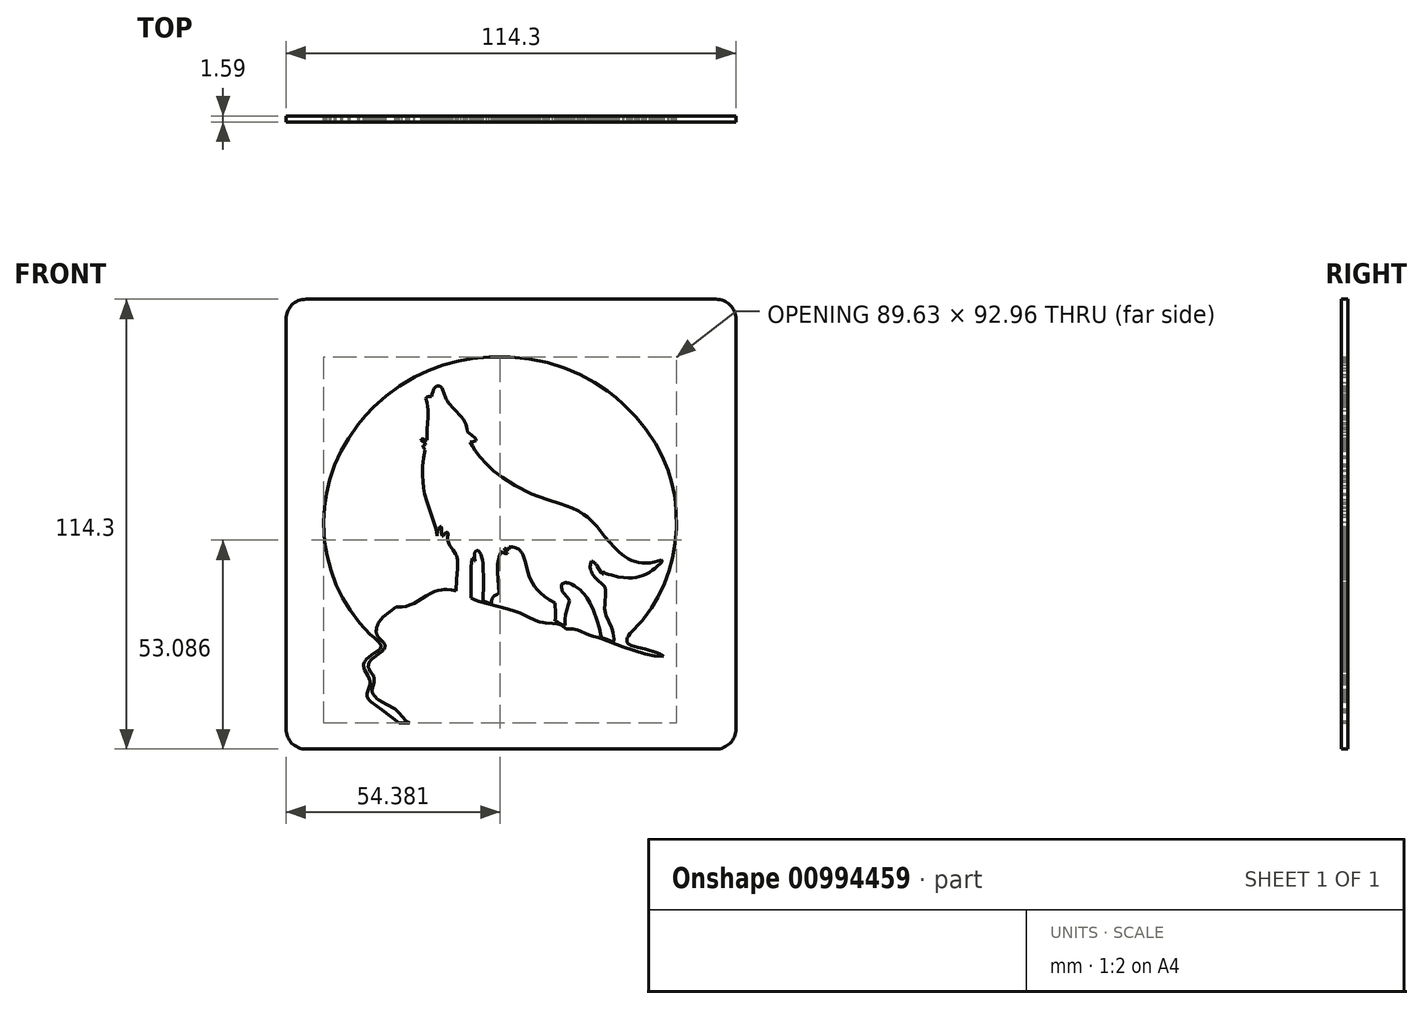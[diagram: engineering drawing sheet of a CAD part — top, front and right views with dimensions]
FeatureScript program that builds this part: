
annotation { "Feature Type Name" : "Feature", "Feature Type Description" : "" }
export const myFeature = defineFeature(function(context is Context, id is Id, definition is map)
    precondition{}
    {
        {
            var Q0;
            Q0=qCreatedBy(makeId("Front.planeOp"),FACE);
            var sketch = newSketch(context, id + "F0", { "sketchPlane" : qUnion([Q0])});
            skLineSegment(sketch, "E0", {"start": v(-50.8, -48.51) * mm, "end": v(-50.61, -48.95) * mm});
            skLineSegment(sketch, "E1", {"start": v(-50.61, -48.95) * mm, "end": v(-50.42, -49.3) * mm});
            skLineSegment(sketch, "E2", {"start": v(-50.42, -49.3) * mm, "end": v(-50.23, -49.58) * mm});
            skLineSegment(sketch, "E3", {"start": v(-50.23, -49.58) * mm, "end": v(-50.05, -49.8) * mm});
            skLineSegment(sketch, "E4", {"start": v(-50.05, -49.8) * mm, "end": v(-49.86, -49.99) * mm});
            skLineSegment(sketch, "E5", {"start": v(-49.86, -49.99) * mm, "end": v(-49.64, -50.16) * mm});
            skLineSegment(sketch, "E6", {"start": v(-49.64, -50.16) * mm, "end": v(-49.41, -50.32) * mm});
            skLineSegment(sketch, "E7", {"start": v(-49.41, -50.32) * mm, "end": v(-49.2, -50.43) * mm});
            skLineSegment(sketch, "E8", {"start": v(-49.2, -50.43) * mm, "end": v(-48.94, -50.55) * mm});
            skLineSegment(sketch, "E9", {"start": v(-48.94, -50.55) * mm, "end": v(-28.45, -50.55) * mm});
            skLineSegment(sketch, "E10", {"start": v(-28.45, -50.55) * mm, "end": v(-32.68, -47.16) * mm});
            skLineSegment(sketch, "E11", {"start": v(-32.68, -47.16) * mm, "end": v(-35.5, -45.2) * mm});
            skLineSegment(sketch, "E12", {"start": v(-35.5, -45.2) * mm, "end": v(-35.9, -44.8) * mm});
            skLineSegment(sketch, "E13", {"start": v(-35.9, -44.8) * mm, "end": v(-36.11, -44.55) * mm});
            skLineSegment(sketch, "E14", {"start": v(-36.11, -44.55) * mm, "end": v(-36.29, -44.28) * mm});
            skLineSegment(sketch, "E15", {"start": v(-36.29, -44.28) * mm, "end": v(-36.43, -44.01) * mm});
            skLineSegment(sketch, "E16", {"start": v(-36.43, -44.01) * mm, "end": v(-36.5, -43.82) * mm});
            skLineSegment(sketch, "E17", {"start": v(-36.5, -43.82) * mm, "end": v(-36.55, -43.63) * mm});
            skLineSegment(sketch, "E18", {"start": v(-36.55, -43.63) * mm, "end": v(-36.58, -43.43) * mm});
            skLineSegment(sketch, "E19", {"start": v(-36.58, -43.43) * mm, "end": v(-36.58, -43.32) * mm});
            skLineSegment(sketch, "E20", {"start": v(-36.58, -43.32) * mm, "end": v(-36.57, -43.15) * mm});
            skLineSegment(sketch, "E21", {"start": v(-36.57, -43.15) * mm, "end": v(-36.54, -42.98) * mm});
            skLineSegment(sketch, "E22", {"start": v(-36.54, -42.98) * mm, "end": v(-36.47, -42.67) * mm});
            skLineSegment(sketch, "E23", {"start": v(-36.47, -42.67) * mm, "end": v(-35.78, -40.74) * mm});
            skLineSegment(sketch, "E24", {"start": v(-35.78, -40.74) * mm, "end": v(-35.74, -40.48) * mm});
            skLineSegment(sketch, "E25", {"start": v(-35.74, -40.48) * mm, "end": v(-35.73, -40.35) * mm});
            skLineSegment(sketch, "E26", {"start": v(-35.73, -40.35) * mm, "end": v(-35.73, -40.22) * mm});
            skLineSegment(sketch, "E27", {"start": v(-35.73, -40.22) * mm, "end": v(-35.74, -40.05) * mm});
            skLineSegment(sketch, "E28", {"start": v(-35.74, -40.05) * mm, "end": v(-35.79, -39.8) * mm});
            skLineSegment(sketch, "E29", {"start": v(-35.79, -39.8) * mm, "end": v(-35.86, -39.53) * mm});
            skLineSegment(sketch, "E30", {"start": v(-35.86, -39.53) * mm, "end": v(-36, -39.18) * mm});
            skLineSegment(sketch, "E31", {"start": v(-36, -39.18) * mm, "end": v(-36.32, -38.57) * mm});
            skLineSegment(sketch, "E32", {"start": v(-36.32, -38.57) * mm, "end": v(-37.15, -37.06) * mm});
            skLineSegment(sketch, "E33", {"start": v(-37.15, -37.06) * mm, "end": v(-37.29, -36.7) * mm});
            skLineSegment(sketch, "E34", {"start": v(-37.29, -36.7) * mm, "end": v(-37.36, -36.44) * mm});
            skLineSegment(sketch, "E35", {"start": v(-37.36, -36.44) * mm, "end": v(-37.41, -36.17) * mm});
            skLineSegment(sketch, "E36", {"start": v(-37.41, -36.17) * mm, "end": v(-37.43, -36) * mm});
            skLineSegment(sketch, "E37", {"start": v(-37.43, -36) * mm, "end": v(-37.42, -35.82) * mm});
            skLineSegment(sketch, "E38", {"start": v(-37.42, -35.82) * mm, "end": v(-37.39, -35.56) * mm});
            skLineSegment(sketch, "E39", {"start": v(-37.39, -35.56) * mm, "end": v(-37.32, -35.3) * mm});
            skLineSegment(sketch, "E40", {"start": v(-37.32, -35.3) * mm, "end": v(-37.21, -35.07) * mm});
            skLineSegment(sketch, "E41", {"start": v(-37.21, -35.07) * mm, "end": v(-37.08, -34.84) * mm});
            skLineSegment(sketch, "E42", {"start": v(-37.08, -34.84) * mm, "end": v(-36.92, -34.62) * mm});
            skLineSegment(sketch, "E43", {"start": v(-36.92, -34.62) * mm, "end": v(-36.65, -34.3) * mm});
            skLineSegment(sketch, "E44", {"start": v(-36.65, -34.3) * mm, "end": v(-36.21, -33.9) * mm});
            skLineSegment(sketch, "E45", {"start": v(-36.21, -33.9) * mm, "end": v(-35.35, -33.26) * mm});
            skLineSegment(sketch, "E46", {"start": v(-35.35, -33.26) * mm, "end": v(-33.7, -32.09) * mm});
            skLineSegment(sketch, "E47", {"start": v(-33.7, -32.09) * mm, "end": v(-33.43, -31.84) * mm});
            skLineSegment(sketch, "E48", {"start": v(-33.43, -31.84) * mm, "end": v(-33.29, -31.68) * mm});
            skLineSegment(sketch, "E49", {"start": v(-33.29, -31.68) * mm, "end": v(-33.17, -31.5) * mm});
            skLineSegment(sketch, "E50", {"start": v(-33.17, -31.5) * mm, "end": v(-33.09, -31.34) * mm});
            skLineSegment(sketch, "E51", {"start": v(-33.09, -31.34) * mm, "end": v(-33.06, -31.25) * mm});
            skLineSegment(sketch, "E52", {"start": v(-33.06, -31.25) * mm, "end": v(-33.03, -31.16) * mm});
            skLineSegment(sketch, "E53", {"start": v(-33.03, -31.16) * mm, "end": v(-33.02, -31.07) * mm});
            skLineSegment(sketch, "E54", {"start": v(-33.02, -31.07) * mm, "end": v(-33.02, -31.02) * mm});
            skLineSegment(sketch, "E55", {"start": v(-33.02, -31.02) * mm, "end": v(-33.02, -30.96) * mm});
            skLineSegment(sketch, "E56", {"start": v(-33.02, -30.96) * mm, "end": v(-33.04, -30.85) * mm});
            skLineSegment(sketch, "E57", {"start": v(-33.04, -30.85) * mm, "end": v(-33.08, -30.73) * mm});
            skLineSegment(sketch, "E58", {"start": v(-33.08, -30.73) * mm, "end": v(-33.13, -30.6) * mm});
            skLineSegment(sketch, "E59", {"start": v(-33.13, -30.6) * mm, "end": v(-33.24, -30.42) * mm});
            skLineSegment(sketch, "E60", {"start": v(-33.24, -30.42) * mm, "end": v(-33.43, -30.16) * mm});
            skLineSegment(sketch, "E61", {"start": v(-33.43, -30.16) * mm, "end": v(-33.8, -29.75) * mm});
            skLineSegment(sketch, "E62", {"start": v(-33.8, -29.75) * mm, "end": v(-34.81, -28.83) * mm});
            skLineSegment(sketch, "E63", {"start": v(-34.81, -28.83) * mm, "end": v(-35.73, -28.03) * mm});
            skLineSegment(sketch, "E64", {"start": v(-35.73, -28.03) * mm, "end": v(-38.4, -25.1) * mm});
            skLineSegment(sketch, "E65", {"start": v(-38.4, -25.1) * mm, "end": v(-40.85, -21.83) * mm});
            skLineSegment(sketch, "E66", {"start": v(-40.85, -21.83) * mm, "end": v(-42.74, -18.74) * mm});
            skLineSegment(sketch, "E67", {"start": v(-42.74, -18.74) * mm, "end": v(-44.38, -15.4) * mm});
            skLineSegment(sketch, "E68", {"start": v(-44.38, -15.4) * mm, "end": v(-45.73, -11.78) * mm});
            skLineSegment(sketch, "E69", {"start": v(-45.73, -11.78) * mm, "end": v(-46.75, -7.92) * mm});
            skLineSegment(sketch, "E70", {"start": v(-46.75, -7.92) * mm, "end": v(-47.3, -4.5) * mm});
            skLineSegment(sketch, "E71", {"start": v(-47.3, -4.5) * mm, "end": v(-47.5, -2.36) * mm});
            skLineSegment(sketch, "E72", {"start": v(-47.5, -2.36) * mm, "end": v(-47.58, 0.6) * mm});
            skLineSegment(sketch, "E73", {"start": v(-47.58, 0.6) * mm, "end": v(-47.4, 4.31) * mm});
            skLineSegment(sketch, "E74", {"start": v(-47.4, 4.31) * mm, "end": v(-46.89, 7.85) * mm});
            skLineSegment(sketch, "E75", {"start": v(-46.89, 7.85) * mm, "end": v(-46.09, 11.2) * mm});
            skLineSegment(sketch, "E76", {"start": v(-46.09, 11.2) * mm, "end": v(-44.8, 15) * mm});
            skLineSegment(sketch, "E77", {"start": v(-44.8, 15) * mm, "end": v(-43.17, 18.54) * mm});
            skLineSegment(sketch, "E78", {"start": v(-43.17, 18.54) * mm, "end": v(-41.28, 21.81) * mm});
            skLineSegment(sketch, "E79", {"start": v(-41.28, 21.81) * mm, "end": v(-38.8, 25.31) * mm});
            skLineSegment(sketch, "E80", {"start": v(-38.8, 25.31) * mm, "end": v(-36.88, 27.6) * mm});
            skLineSegment(sketch, "E81", {"start": v(-36.88, 27.6) * mm, "end": v(-34.88, 29.72) * mm});
            skLineSegment(sketch, "E82", {"start": v(-34.88, 29.72) * mm, "end": v(-31.75, 32.55) * mm});
            skLineSegment(sketch, "E83", {"start": v(-31.75, 32.55) * mm, "end": v(-28.26, 35.12) * mm});
            skLineSegment(sketch, "E84", {"start": v(-28.26, 35.12) * mm, "end": v(-24.44, 37.37) * mm});
            skLineSegment(sketch, "E85", {"start": v(-24.44, 37.37) * mm, "end": v(-20.93, 39.02) * mm});
            skLineSegment(sketch, "E86", {"start": v(-20.93, 39.02) * mm, "end": v(-17.2, 40.39) * mm});
            skLineSegment(sketch, "E87", {"start": v(-17.2, 40.39) * mm, "end": v(-13.27, 41.43) * mm});
            skLineSegment(sketch, "E88", {"start": v(-13.27, 41.43) * mm, "end": v(-9.85, 42.03) * mm});
            skLineSegment(sketch, "E89", {"start": v(-9.85, 42.03) * mm, "end": v(-5.59, 42.42) * mm});
            skLineSegment(sketch, "E90", {"start": v(-5.59, 42.42) * mm, "end": v(-0.25, 42.41) * mm});
            skLineSegment(sketch, "E91", {"start": v(-0.25, 42.41) * mm, "end": v(4.72, 41.93) * mm});
            skLineSegment(sketch, "E92", {"start": v(4.72, 41.93) * mm, "end": v(9.34, 41.01) * mm});
            skLineSegment(sketch, "E93", {"start": v(9.34, 41.01) * mm, "end": v(13.62, 39.7) * mm});
            skLineSegment(sketch, "E94", {"start": v(13.62, 39.7) * mm, "end": v(17.58, 38.03) * mm});
            skLineSegment(sketch, "E95", {"start": v(17.58, 38.03) * mm, "end": v(21.23, 36.04) * mm});
            skLineSegment(sketch, "E96", {"start": v(21.23, 36.04) * mm, "end": v(24.58, 33.78) * mm});
            skLineSegment(sketch, "E97", {"start": v(24.58, 33.78) * mm, "end": v(26.66, 32.13) * mm});
            skLineSegment(sketch, "E98", {"start": v(26.66, 32.13) * mm, "end": v(28.62, 30.4) * mm});
            skLineSegment(sketch, "E99", {"start": v(28.62, 30.4) * mm, "end": v(31.78, 27.16) * mm});
            skLineSegment(sketch, "E100", {"start": v(31.78, 27.16) * mm, "end": v(34.36, 24) * mm});
            skLineSegment(sketch, "E101", {"start": v(34.36, 24) * mm, "end": v(36.69, 20.52) * mm});
            skLineSegment(sketch, "E102", {"start": v(36.69, 20.52) * mm, "end": v(38.43, 17.28) * mm});
            skLineSegment(sketch, "E103", {"start": v(38.43, 17.28) * mm, "end": v(39.88, 13.8) * mm});
            skLineSegment(sketch, "E104", {"start": v(39.88, 13.8) * mm, "end": v(40.84, 10.72) * mm});
            skLineSegment(sketch, "E105", {"start": v(40.84, 10.72) * mm, "end": v(41.54, 7.45) * mm});
            skLineSegment(sketch, "E106", {"start": v(41.54, 7.45) * mm, "end": v(41.82, 5.4) * mm});
            skLineSegment(sketch, "E107", {"start": v(41.82, 5.4) * mm, "end": v(42, 3.3) * mm});
            skLineSegment(sketch, "E108", {"start": v(42, 3.3) * mm, "end": v(42.05, -0.92) * mm});
            skLineSegment(sketch, "E109", {"start": v(42.05, -0.92) * mm, "end": v(41.73, -4.87) * mm});
            skLineSegment(sketch, "E110", {"start": v(41.73, -4.87) * mm, "end": v(41.1, -8.54) * mm});
            skLineSegment(sketch, "E111", {"start": v(41.1, -8.54) * mm, "end": v(40.17, -11.96) * mm});
            skLineSegment(sketch, "E112", {"start": v(40.17, -11.96) * mm, "end": v(39, -15.13) * mm});
            skLineSegment(sketch, "E113", {"start": v(39, -15.13) * mm, "end": v(37.35, -18.55) * mm});
            skLineSegment(sketch, "E114", {"start": v(37.35, -18.55) * mm, "end": v(35.75, -21.24) * mm});
            skLineSegment(sketch, "E115", {"start": v(35.75, -21.24) * mm, "end": v(33.7, -24.13) * mm});
            skLineSegment(sketch, "E116", {"start": v(33.7, -24.13) * mm, "end": v(33.34, -24.55) * mm});
            skLineSegment(sketch, "E117", {"start": v(33.34, -24.55) * mm, "end": v(30.29, -27.79) * mm});
            skLineSegment(sketch, "E118", {"start": v(30.29, -27.79) * mm, "end": v(29.84, -28.43) * mm});
            skLineSegment(sketch, "E119", {"start": v(29.84, -28.43) * mm, "end": v(29.64, -28.8) * mm});
            skLineSegment(sketch, "E120", {"start": v(29.64, -28.8) * mm, "end": v(29.54, -29.03) * mm});
            skLineSegment(sketch, "E121", {"start": v(29.54, -29.03) * mm, "end": v(29.47, -29.26) * mm});
            skLineSegment(sketch, "E122", {"start": v(29.47, -29.26) * mm, "end": v(29.44, -29.48) * mm});
            skLineSegment(sketch, "E123", {"start": v(29.44, -29.48) * mm, "end": v(29.43, -29.7) * mm});
            skLineSegment(sketch, "E124", {"start": v(29.43, -29.7) * mm, "end": v(29.44, -29.8) * mm});
            skLineSegment(sketch, "E125", {"start": v(29.44, -29.8) * mm, "end": v(29.46, -29.89) * mm});
            skLineSegment(sketch, "E126", {"start": v(29.46, -29.89) * mm, "end": v(29.49, -29.95) * mm});
            skLineSegment(sketch, "E127", {"start": v(29.49, -29.95) * mm, "end": v(29.51, -30.01) * mm});
            skLineSegment(sketch, "E128", {"start": v(29.51, -30.01) * mm, "end": v(29.58, -30.13) * mm});
            skLineSegment(sketch, "E129", {"start": v(29.58, -30.13) * mm, "end": v(29.68, -30.24) * mm});
            skLineSegment(sketch, "E130", {"start": v(29.68, -30.24) * mm, "end": v(29.8, -30.35) * mm});
            skLineSegment(sketch, "E131", {"start": v(29.8, -30.35) * mm, "end": v(29.93, -30.45) * mm});
            skLineSegment(sketch, "E132", {"start": v(29.93, -30.45) * mm, "end": v(30.17, -30.6) * mm});
            skLineSegment(sketch, "E133", {"start": v(30.17, -30.6) * mm, "end": v(30.53, -30.77) * mm});
            skLineSegment(sketch, "E134", {"start": v(30.53, -30.77) * mm, "end": v(32.31, -31.33) * mm});
            skLineSegment(sketch, "E135", {"start": v(32.31, -31.33) * mm, "end": v(34.04, -31.75) * mm});
            skLineSegment(sketch, "E136", {"start": v(34.04, -31.75) * mm, "end": v(37.21, -32.69) * mm});
            skLineSegment(sketch, "E137", {"start": v(37.21, -32.69) * mm, "end": v(37.81, -32.96) * mm});
            skLineSegment(sketch, "E138", {"start": v(37.81, -32.96) * mm, "end": v(38.21, -33.18) * mm});
            skLineSegment(sketch, "E139", {"start": v(38.21, -33.18) * mm, "end": v(38.5, -33.39) * mm});
            skLineSegment(sketch, "E140", {"start": v(38.5, -33.39) * mm, "end": v(38.78, -33.61) * mm});
            skLineSegment(sketch, "E141", {"start": v(38.78, -33.61) * mm, "end": v(36.53, -33.44) * mm});
            skLineSegment(sketch, "E142", {"start": v(36.53, -33.44) * mm, "end": v(34.08, -33.02) * mm});
            skLineSegment(sketch, "E143", {"start": v(34.08, -33.02) * mm, "end": v(28.44, -31.21) * mm});
            skLineSegment(sketch, "E144", {"start": v(28.44, -31.21) * mm, "end": v(22.86, -29.04) * mm});
            skLineSegment(sketch, "E145", {"start": v(22.86, -29.04) * mm, "end": v(22.14, -28.83) * mm});
            skLineSegment(sketch, "E146", {"start": v(22.14, -28.83) * mm, "end": v(20.96, -28.56) * mm});
            skLineSegment(sketch, "E147", {"start": v(20.96, -28.56) * mm, "end": v(19.81, -28.2) * mm});
            skLineSegment(sketch, "E148", {"start": v(19.81, -28.2) * mm, "end": v(16.92, -26.9) * mm});
            skLineSegment(sketch, "E149", {"start": v(16.92, -26.9) * mm, "end": v(16.34, -26.75) * mm});
            skLineSegment(sketch, "E150", {"start": v(16.34, -26.75) * mm, "end": v(15.72, -26.64) * mm});
            skLineSegment(sketch, "E151", {"start": v(15.72, -26.64) * mm, "end": v(15.2, -26.6) * mm});
            skLineSegment(sketch, "E152", {"start": v(15.2, -26.6) * mm, "end": v(14.64, -26.6) * mm});
            skLineSegment(sketch, "E153", {"start": v(14.64, -26.6) * mm, "end": v(14.05, -26.67) * mm});
            skLineSegment(sketch, "E154", {"start": v(14.05, -26.67) * mm, "end": v(13.73, -26.33) * mm});
            skLineSegment(sketch, "E155", {"start": v(13.73, -26.33) * mm, "end": v(13.48, -26.11) * mm});
            skLineSegment(sketch, "E156", {"start": v(13.48, -26.11) * mm, "end": v(13.23, -25.93) * mm});
            skLineSegment(sketch, "E157", {"start": v(13.23, -25.93) * mm, "end": v(12.97, -25.78) * mm});
            skLineSegment(sketch, "E158", {"start": v(12.97, -25.78) * mm, "end": v(12.7, -25.66) * mm});
            skLineSegment(sketch, "E159", {"start": v(12.7, -25.66) * mm, "end": v(12.33, -25.53) * mm});
            skLineSegment(sketch, "E160", {"start": v(12.33, -25.53) * mm, "end": v(11.83, -25.42) * mm});
            skLineSegment(sketch, "E161", {"start": v(11.83, -25.42) * mm, "end": v(10.52, -25.28) * mm});
            skLineSegment(sketch, "E162", {"start": v(10.52, -25.28) * mm, "end": v(8.8, -25.15) * mm});
            skLineSegment(sketch, "E163", {"start": v(8.8, -25.15) * mm, "end": v(8.12, -25.04) * mm});
            skLineSegment(sketch, "E164", {"start": v(8.12, -25.04) * mm, "end": v(7.31, -24.84) * mm});
            skLineSegment(sketch, "E165", {"start": v(7.31, -24.84) * mm, "end": v(6.26, -24.47) * mm});
            skLineSegment(sketch, "E166", {"start": v(6.26, -24.47) * mm, "end": v(4.34, -23.58) * mm});
            skLineSegment(sketch, "E167", {"start": v(4.34, -23.58) * mm, "end": v(2.37, -22.6) * mm});
            skLineSegment(sketch, "E168", {"start": v(2.37, -22.6) * mm, "end": v(1.18, -22.12) * mm});
            skLineSegment(sketch, "E169", {"start": v(1.18, -22.12) * mm, "end": v(-0.85, -21.5) * mm});
            skLineSegment(sketch, "E170", {"start": v(-0.85, -21.5) * mm, "end": v(-8.14, -19.64) * mm});
            skLineSegment(sketch, "E171", {"start": v(-8.14, -19.64) * mm, "end": v(-9.07, -19.27) * mm});
            skLineSegment(sketch, "E172", {"start": v(-9.07, -19.27) * mm, "end": v(-10.16, -18.71) * mm});
            skLineSegment(sketch, "E173", {"start": v(-10.16, -18.71) * mm, "end": v(-10.11, -10.8) * mm});
            skLineSegment(sketch, "E174", {"start": v(-10.11, -10.8) * mm, "end": v(-10, -9.83) * mm});
            skLineSegment(sketch, "E175", {"start": v(-10, -9.83) * mm, "end": v(-9.82, -8.72) * mm});
            skLineSegment(sketch, "E176", {"start": v(-9.82, -8.72) * mm, "end": v(-9.78, -8.73) * mm});
            skLineSegment(sketch, "E177", {"start": v(-9.78, -8.73) * mm, "end": v(-9.73, -8.74) * mm});
            skLineSegment(sketch, "E178", {"start": v(-9.73, -8.74) * mm, "end": v(-9.7, -8.76) * mm});
            skLineSegment(sketch, "E179", {"start": v(-9.7, -8.76) * mm, "end": v(-9.66, -8.78) * mm});
            skLineSegment(sketch, "E180", {"start": v(-9.66, -8.78) * mm, "end": v(-9.63, -8.8) * mm});
            skLineSegment(sketch, "E181", {"start": v(-9.63, -8.8) * mm, "end": v(-9.6, -8.82) * mm});
            skLineSegment(sketch, "E182", {"start": v(-9.6, -8.82) * mm, "end": v(-9.56, -8.86) * mm});
            skLineSegment(sketch, "E183", {"start": v(-9.56, -8.86) * mm, "end": v(-9.52, -8.9) * mm});
            skLineSegment(sketch, "E184", {"start": v(-9.52, -8.9) * mm, "end": v(-9.47, -8.99) * mm});
            skLineSegment(sketch, "E185", {"start": v(-9.47, -8.99) * mm, "end": v(-9.3, -9.26) * mm});
            skLineSegment(sketch, "E186", {"start": v(-9.3, -9.26) * mm, "end": v(-9.27, -9.3) * mm});
            skLineSegment(sketch, "E187", {"start": v(-9.27, -9.3) * mm, "end": v(-9.22, -9.34) * mm});
            skLineSegment(sketch, "E188", {"start": v(-9.22, -9.34) * mm, "end": v(-9.2, -9.37) * mm});
            skLineSegment(sketch, "E189", {"start": v(-9.2, -9.37) * mm, "end": v(-9.18, -9.38) * mm});
            skLineSegment(sketch, "E190", {"start": v(-9.18, -9.38) * mm, "end": v(-9.14, -9.4) * mm});
            skLineSegment(sketch, "E191", {"start": v(-9.14, -9.4) * mm, "end": v(-9.29, -8.42) * mm});
            skLineSegment(sketch, "E192", {"start": v(-9.29, -8.42) * mm, "end": v(-9.3, -8) * mm});
            skLineSegment(sketch, "E193", {"start": v(-9.3, -8) * mm, "end": v(-9.3, -7.72) * mm});
            skLineSegment(sketch, "E194", {"start": v(-9.3, -7.72) * mm, "end": v(-9.26, -7.52) * mm});
            skLineSegment(sketch, "E195", {"start": v(-9.26, -7.52) * mm, "end": v(-9.22, -7.34) * mm});
            skLineSegment(sketch, "E196", {"start": v(-9.22, -7.34) * mm, "end": v(-9.17, -7.23) * mm});
            skLineSegment(sketch, "E197", {"start": v(-9.17, -7.23) * mm, "end": v(-9.12, -7.12) * mm});
            skLineSegment(sketch, "E198", {"start": v(-9.12, -7.12) * mm, "end": v(-9.06, -7.03) * mm});
            skLineSegment(sketch, "E199", {"start": v(-9.06, -7.03) * mm, "end": v(-8.99, -6.95) * mm});
            skLineSegment(sketch, "E200", {"start": v(-8.99, -6.95) * mm, "end": v(-8.9, -6.87) * mm});
            skLineSegment(sketch, "E201", {"start": v(-8.9, -6.87) * mm, "end": v(-8.81, -6.8) * mm});
            skLineSegment(sketch, "E202", {"start": v(-8.81, -6.8) * mm, "end": v(-8.7, -6.76) * mm});
            skLineSegment(sketch, "E203", {"start": v(-8.7, -6.76) * mm, "end": v(-8.58, -6.72) * mm});
            skLineSegment(sketch, "E204", {"start": v(-8.58, -6.72) * mm, "end": v(-8.45, -6.7) * mm});
            skLineSegment(sketch, "E205", {"start": v(-8.45, -6.7) * mm, "end": v(-8.3, -6.69) * mm});
            skLineSegment(sketch, "E206", {"start": v(-8.3, -6.69) * mm, "end": v(-8.05, -7) * mm});
            skLineSegment(sketch, "E207", {"start": v(-8.05, -7) * mm, "end": v(-7.83, -7.35) * mm});
            skLineSegment(sketch, "E208", {"start": v(-7.83, -7.35) * mm, "end": v(-7.64, -7.73) * mm});
            skLineSegment(sketch, "E209", {"start": v(-7.64, -7.73) * mm, "end": v(-7.4, -8.36) * mm});
            skLineSegment(sketch, "E210", {"start": v(-7.4, -8.36) * mm, "end": v(-7.22, -9.05) * mm});
            skLineSegment(sketch, "E211", {"start": v(-7.22, -9.05) * mm, "end": v(-7.04, -10.04) * mm});
            skLineSegment(sketch, "E212", {"start": v(-7.04, -10.04) * mm, "end": v(-6.94, -14.85) * mm});
            skLineSegment(sketch, "E213", {"start": v(-6.94, -14.85) * mm, "end": v(-7.11, -19.56) * mm});
            skLineSegment(sketch, "E214", {"start": v(-7.11, -19.56) * mm, "end": v(-4.91, -20.24) * mm});
            skLineSegment(sketch, "E215", {"start": v(-4.91, -20.24) * mm, "end": v(-4.94, -19.84) * mm});
            skLineSegment(sketch, "E216", {"start": v(-4.94, -19.84) * mm, "end": v(-4.94, -19.57) * mm});
            skLineSegment(sketch, "E217", {"start": v(-4.94, -19.57) * mm, "end": v(-4.9, -19.33) * mm});
            skLineSegment(sketch, "E218", {"start": v(-4.9, -19.33) * mm, "end": v(-4.85, -19.1) * mm});
            skLineSegment(sketch, "E219", {"start": v(-4.85, -19.1) * mm, "end": v(-4.78, -18.9) * mm});
            skLineSegment(sketch, "E220", {"start": v(-4.78, -18.9) * mm, "end": v(-4.68, -18.73) * mm});
            skLineSegment(sketch, "E221", {"start": v(-4.68, -18.73) * mm, "end": v(-4.57, -18.57) * mm});
            skLineSegment(sketch, "E222", {"start": v(-4.57, -18.57) * mm, "end": v(-4.44, -18.42) * mm});
            skLineSegment(sketch, "E223", {"start": v(-4.44, -18.42) * mm, "end": v(-4.3, -18.29) * mm});
            skLineSegment(sketch, "E224", {"start": v(-4.3, -18.29) * mm, "end": v(-4.1, -18.13) * mm});
            skLineSegment(sketch, "E225", {"start": v(-4.1, -18.13) * mm, "end": v(-3.58, -17.81) * mm});
            skLineSegment(sketch, "E226", {"start": v(-3.58, -17.81) * mm, "end": v(-3.05, -17.53) * mm});
            skLineSegment(sketch, "E227", {"start": v(-3.05, -17.53) * mm, "end": v(-3.42, -12.23) * mm});
            skLineSegment(sketch, "E228", {"start": v(-3.42, -12.23) * mm, "end": v(-3.35, -10.2) * mm});
            skLineSegment(sketch, "E229", {"start": v(-3.35, -10.2) * mm, "end": v(-3.18, -8.96) * mm});
            skLineSegment(sketch, "E230", {"start": v(-3.18, -8.96) * mm, "end": v(-3, -8.2) * mm});
            skLineSegment(sketch, "E231", {"start": v(-3, -8.2) * mm, "end": v(-2.83, -7.67) * mm});
            skLineSegment(sketch, "E232", {"start": v(-2.83, -7.67) * mm, "end": v(-2.54, -7.03) * mm});
            skLineSegment(sketch, "E233", {"start": v(-2.54, -7.03) * mm, "end": v(-2.45, -7.05) * mm});
            skLineSegment(sketch, "E234", {"start": v(-2.45, -7.05) * mm, "end": v(-2.32, -7.1) * mm});
            skLineSegment(sketch, "E235", {"start": v(-2.32, -7.1) * mm, "end": v(-1.45, -7.46) * mm});
            skLineSegment(sketch, "E236", {"start": v(-1.45, -7.46) * mm, "end": v(-1.34, -7.48) * mm});
            skLineSegment(sketch, "E237", {"start": v(-1.34, -7.48) * mm, "end": v(-1.23, -7.5) * mm});
            skLineSegment(sketch, "E238", {"start": v(-1.23, -7.5) * mm, "end": v(-1.17, -7.5) * mm});
            skLineSegment(sketch, "E239", {"start": v(-1.17, -7.5) * mm, "end": v(-1.1, -7.5) * mm});
            skLineSegment(sketch, "E240", {"start": v(-1.1, -7.5) * mm, "end": v(-1.04, -7.48) * mm});
            skLineSegment(sketch, "E241", {"start": v(-1.04, -7.48) * mm, "end": v(-0.98, -7.46) * mm});
            skLineSegment(sketch, "E242", {"start": v(-0.98, -7.46) * mm, "end": v(-0.93, -7.43) * mm});
            skLineSegment(sketch, "E243", {"start": v(-0.93, -7.43) * mm, "end": v(-0.9, -7.41) * mm});
            skLineSegment(sketch, "E244", {"start": v(-0.9, -7.41) * mm, "end": v(-0.85, -7.37) * mm});
            skLineSegment(sketch, "E245", {"start": v(-0.85, -7.37) * mm, "end": v(-0.9, -7.35) * mm});
            skLineSegment(sketch, "E246", {"start": v(-0.9, -7.35) * mm, "end": v(-0.94, -7.32) * mm});
            skLineSegment(sketch, "E247", {"start": v(-0.94, -7.32) * mm, "end": v(-1.01, -7.27) * mm});
            skLineSegment(sketch, "E248", {"start": v(-1.01, -7.27) * mm, "end": v(-1.11, -7.19) * mm});
            skLineSegment(sketch, "E249", {"start": v(-1.11, -7.19) * mm, "end": v(-1.2, -7.09) * mm});
            skLineSegment(sketch, "E250", {"start": v(-1.2, -7.09) * mm, "end": v(-1.32, -6.95) * mm});
            skLineSegment(sketch, "E251", {"start": v(-1.32, -6.95) * mm, "end": v(-1.42, -6.8) * mm});
            skLineSegment(sketch, "E252", {"start": v(-1.42, -6.8) * mm, "end": v(-1.5, -6.64) * mm});
            skLineSegment(sketch, "E253", {"start": v(-1.5, -6.64) * mm, "end": v(-1.55, -6.53) * mm});
            skLineSegment(sketch, "E254", {"start": v(-1.55, -6.53) * mm, "end": v(-1.57, -6.44) * mm});
            skLineSegment(sketch, "E255", {"start": v(-1.57, -6.44) * mm, "end": v(-1.58, -6.4) * mm});
            skLineSegment(sketch, "E256", {"start": v(-1.58, -6.4) * mm, "end": v(-1.58, -6.34) * mm});
            skLineSegment(sketch, "E257", {"start": v(-1.58, -6.34) * mm, "end": v(-1.58, -6.3) * mm});
            skLineSegment(sketch, "E258", {"start": v(-1.58, -6.3) * mm, "end": v(-1.57, -6.26) * mm});
            skLineSegment(sketch, "E259", {"start": v(-1.57, -6.26) * mm, "end": v(-1.57, -6.24) * mm});
            skLineSegment(sketch, "E260", {"start": v(-1.57, -6.24) * mm, "end": v(-1.56, -6.22) * mm});
            skLineSegment(sketch, "E261", {"start": v(-1.56, -6.22) * mm, "end": v(-1.55, -6.2) * mm});
            skLineSegment(sketch, "E262", {"start": v(-1.55, -6.2) * mm, "end": v(-1.54, -6.2) * mm});
            skLineSegment(sketch, "E263", {"start": v(-1.54, -6.2) * mm, "end": v(-1.52, -6.18) * mm});
            skLineSegment(sketch, "E264", {"start": v(-1.52, -6.18) * mm, "end": v(-0.94, -6.38) * mm});
            skLineSegment(sketch, "E265", {"start": v(-0.94, -6.38) * mm, "end": v(-0.77, -6.41) * mm});
            skLineSegment(sketch, "E266", {"start": v(-0.77, -6.41) * mm, "end": v(-0.69, -6.42) * mm});
            skLineSegment(sketch, "E267", {"start": v(-0.69, -6.42) * mm, "end": v(-0.64, -6.42) * mm});
            skLineSegment(sketch, "E268", {"start": v(-0.64, -6.42) * mm, "end": v(-0.6, -6.41) * mm});
            skLineSegment(sketch, "E269", {"start": v(-0.6, -6.41) * mm, "end": v(-0.56, -6.4) * mm});
            skLineSegment(sketch, "E270", {"start": v(-0.56, -6.4) * mm, "end": v(-0.55, -6.4) * mm});
            skLineSegment(sketch, "E271", {"start": v(-0.55, -6.4) * mm, "end": v(-0.53, -6.39) * mm});
            skLineSegment(sketch, "E272", {"start": v(-0.53, -6.39) * mm, "end": v(-0.52, -6.38) * mm});
            skLineSegment(sketch, "E273", {"start": v(-0.52, -6.38) * mm, "end": v(-0.5, -6.36) * mm});
            skLineSegment(sketch, "E274", {"start": v(-0.5, -6.36) * mm, "end": v(-0.5, -6.35) * mm});
            skLineSegment(sketch, "E275", {"start": v(-0.5, -6.35) * mm, "end": v(-0.5, -6.34) * mm});
            skLineSegment(sketch, "E276", {"start": v(-0.5, -6.34) * mm, "end": v(-0.48, -6.32) * mm});
            skLineSegment(sketch, "E277", {"start": v(-0.48, -6.32) * mm, "end": v(-0.47, -6.3) * mm});
            skLineSegment(sketch, "E278", {"start": v(-0.47, -6.3) * mm, "end": v(-0.47, -6.27) * mm});
            skLineSegment(sketch, "E279", {"start": v(-0.47, -6.27) * mm, "end": v(-0.46, -6.23) * mm});
            skLineSegment(sketch, "E280", {"start": v(-0.46, -6.23) * mm, "end": v(-0.46, -6.18) * mm});
            skLineSegment(sketch, "E281", {"start": v(-0.46, -6.18) * mm, "end": v(-0.46, -6.1) * mm});
            skLineSegment(sketch, "E282", {"start": v(-0.46, -6.1) * mm, "end": v(-0.48, -6) * mm});
            skLineSegment(sketch, "E283", {"start": v(-0.48, -6) * mm, "end": v(-0.5, -5.84) * mm});
            skLineSegment(sketch, "E284", {"start": v(-0.5, -5.84) * mm, "end": v(0, -5.82) * mm});
            skLineSegment(sketch, "E285", {"start": v(0, -5.82) * mm, "end": v(0.45, -5.84) * mm});
            skLineSegment(sketch, "E286", {"start": v(0.45, -5.84) * mm, "end": v(0.86, -5.9) * mm});
            skLineSegment(sketch, "E287", {"start": v(0.86, -5.9) * mm, "end": v(1.24, -6.01) * mm});
            skLineSegment(sketch, "E288", {"start": v(1.24, -6.01) * mm, "end": v(1.58, -6.16) * mm});
            skLineSegment(sketch, "E289", {"start": v(1.58, -6.16) * mm, "end": v(1.89, -6.34) * mm});
            skLineSegment(sketch, "E290", {"start": v(1.89, -6.34) * mm, "end": v(2.16, -6.55) * mm});
            skLineSegment(sketch, "E291", {"start": v(2.16, -6.55) * mm, "end": v(2.4, -6.8) * mm});
            skLineSegment(sketch, "E292", {"start": v(2.4, -6.8) * mm, "end": v(2.63, -7.06) * mm});
            skLineSegment(sketch, "E293", {"start": v(2.63, -7.06) * mm, "end": v(2.83, -7.36) * mm});
            skLineSegment(sketch, "E294", {"start": v(2.83, -7.36) * mm, "end": v(3.09, -7.84) * mm});
            skLineSegment(sketch, "E295", {"start": v(3.09, -7.84) * mm, "end": v(3.37, -8.55) * mm});
            skLineSegment(sketch, "E296", {"start": v(3.37, -8.55) * mm, "end": v(3.7, -9.72) * mm});
            skLineSegment(sketch, "E297", {"start": v(3.7, -9.72) * mm, "end": v(4.07, -11.36) * mm});
            skLineSegment(sketch, "E298", {"start": v(4.07, -11.36) * mm, "end": v(4.57, -13.12) * mm});
            skLineSegment(sketch, "E299", {"start": v(4.57, -13.12) * mm, "end": v(4.98, -14.1) * mm});
            skLineSegment(sketch, "E300", {"start": v(4.98, -14.1) * mm, "end": v(5.46, -15) * mm});
            skLineSegment(sketch, "E301", {"start": v(5.46, -15) * mm, "end": v(6, -15.82) * mm});
            skLineSegment(sketch, "E302", {"start": v(6, -15.82) * mm, "end": v(6.72, -16.72) * mm});
            skLineSegment(sketch, "E303", {"start": v(6.72, -16.72) * mm, "end": v(7.52, -17.53) * mm});
            skLineSegment(sketch, "E304", {"start": v(7.52, -17.53) * mm, "end": v(8.54, -18.38) * mm});
            skLineSegment(sketch, "E305", {"start": v(8.54, -18.38) * mm, "end": v(9.8, -19.26) * mm});
            skLineSegment(sketch, "E306", {"start": v(9.8, -19.26) * mm, "end": v(11.18, -20.07) * mm});
            skLineSegment(sketch, "E307", {"start": v(11.18, -20.07) * mm, "end": v(11.34, -22.83) * mm});
            skLineSegment(sketch, "E308", {"start": v(11.34, -22.83) * mm, "end": v(11.3, -23.74) * mm});
            skLineSegment(sketch, "E309", {"start": v(11.3, -23.74) * mm, "end": v(11.18, -24.64) * mm});
            skLineSegment(sketch, "E310", {"start": v(11.18, -24.64) * mm, "end": v(11.29, -24.66) * mm});
            skLineSegment(sketch, "E311", {"start": v(11.29, -24.66) * mm, "end": v(11.4, -24.69) * mm});
            skLineSegment(sketch, "E312", {"start": v(11.4, -24.69) * mm, "end": v(11.57, -24.75) * mm});
            skLineSegment(sketch, "E313", {"start": v(11.57, -24.75) * mm, "end": v(11.8, -24.86) * mm});
            skLineSegment(sketch, "E314", {"start": v(11.8, -24.86) * mm, "end": v(12.34, -25.2) * mm});
            skLineSegment(sketch, "E315", {"start": v(12.34, -25.2) * mm, "end": v(13.06, -25.64) * mm});
            skLineSegment(sketch, "E316", {"start": v(13.06, -25.64) * mm, "end": v(13.2, -25.71) * mm});
            skLineSegment(sketch, "E317", {"start": v(13.2, -25.71) * mm, "end": v(13.3, -25.74) * mm});
            skLineSegment(sketch, "E318", {"start": v(13.3, -25.74) * mm, "end": v(13.38, -25.77) * mm});
            skLineSegment(sketch, "E319", {"start": v(13.38, -25.77) * mm, "end": v(13.46, -25.77) * mm});
            skLineSegment(sketch, "E320", {"start": v(13.46, -25.77) * mm, "end": v(13.5, -25.77) * mm});
            skLineSegment(sketch, "E321", {"start": v(13.5, -25.77) * mm, "end": v(13.53, -25.77) * mm});
            skLineSegment(sketch, "E322", {"start": v(13.53, -25.77) * mm, "end": v(13.57, -25.76) * mm});
            skLineSegment(sketch, "E323", {"start": v(13.57, -25.76) * mm, "end": v(13.6, -25.75) * mm});
            skLineSegment(sketch, "E324", {"start": v(13.6, -25.75) * mm, "end": v(13.63, -25.73) * mm});
            skLineSegment(sketch, "E325", {"start": v(13.63, -25.73) * mm, "end": v(13.66, -25.71) * mm});
            skLineSegment(sketch, "E326", {"start": v(13.66, -25.71) * mm, "end": v(13.69, -25.69) * mm});
            skLineSegment(sketch, "E327", {"start": v(13.69, -25.69) * mm, "end": v(13.72, -25.66) * mm});
            skLineSegment(sketch, "E328", {"start": v(13.72, -25.66) * mm, "end": v(13.76, -24.24) * mm});
            skLineSegment(sketch, "E329", {"start": v(13.76, -24.24) * mm, "end": v(13.92, -22.95) * mm});
            skLineSegment(sketch, "E330", {"start": v(13.92, -22.95) * mm, "end": v(14.2, -21.63) * mm});
            skLineSegment(sketch, "E331", {"start": v(14.2, -21.63) * mm, "end": v(14.5, -20.62) * mm});
            skLineSegment(sketch, "E332", {"start": v(14.5, -20.62) * mm, "end": v(14.9, -19.56) * mm});
            skLineSegment(sketch, "E333", {"start": v(14.9, -19.56) * mm, "end": v(14.79, -19.3) * mm});
            skLineSegment(sketch, "E334", {"start": v(14.79, -19.3) * mm, "end": v(14.65, -19.06) * mm});
            skLineSegment(sketch, "E335", {"start": v(14.65, -19.06) * mm, "end": v(14.45, -18.76) * mm});
            skLineSegment(sketch, "E336", {"start": v(14.45, -18.76) * mm, "end": v(13.27, -17.3) * mm});
            skLineSegment(sketch, "E337", {"start": v(13.27, -17.3) * mm, "end": v(13.14, -17.06) * mm});
            skLineSegment(sketch, "E338", {"start": v(13.14, -17.06) * mm, "end": v(13.03, -16.8) * mm});
            skLineSegment(sketch, "E339", {"start": v(13.03, -16.8) * mm, "end": v(12.94, -16.51) * mm});
            skLineSegment(sketch, "E340", {"start": v(12.94, -16.51) * mm, "end": v(12.88, -16.2) * mm});
            skLineSegment(sketch, "E341", {"start": v(12.88, -16.2) * mm, "end": v(12.85, -15.85) * mm});
            skLineSegment(sketch, "E342", {"start": v(12.85, -15.85) * mm, "end": v(12.85, -15.6) * mm});
            skLineSegment(sketch, "E343", {"start": v(12.85, -15.6) * mm, "end": v(12.87, -15.32) * mm});
            skLineSegment(sketch, "E344", {"start": v(12.87, -15.32) * mm, "end": v(13.03, -15.16) * mm});
            skLineSegment(sketch, "E345", {"start": v(13.03, -15.16) * mm, "end": v(13.2, -15.04) * mm});
            skLineSegment(sketch, "E346", {"start": v(13.2, -15.04) * mm, "end": v(13.4, -14.95) * mm});
            skLineSegment(sketch, "E347", {"start": v(13.4, -14.95) * mm, "end": v(13.6, -14.89) * mm});
            skLineSegment(sketch, "E348", {"start": v(13.6, -14.89) * mm, "end": v(13.83, -14.86) * mm});
            skLineSegment(sketch, "E349", {"start": v(13.83, -14.86) * mm, "end": v(14.05, -14.86) * mm});
            skLineSegment(sketch, "E350", {"start": v(14.05, -14.86) * mm, "end": v(14.29, -14.88) * mm});
            skLineSegment(sketch, "E351", {"start": v(14.29, -14.88) * mm, "end": v(14.65, -14.96) * mm});
            skLineSegment(sketch, "E352", {"start": v(14.65, -14.96) * mm, "end": v(15.03, -15.08) * mm});
            skLineSegment(sketch, "E353", {"start": v(15.03, -15.08) * mm, "end": v(15.53, -15.3) * mm});
            skLineSegment(sketch, "E354", {"start": v(15.53, -15.3) * mm, "end": v(16.15, -15.65) * mm});
            skLineSegment(sketch, "E355", {"start": v(16.15, -15.65) * mm, "end": v(16.96, -16.2) * mm});
            skLineSegment(sketch, "E356", {"start": v(16.96, -16.2) * mm, "end": v(17.64, -16.75) * mm});
            skLineSegment(sketch, "E357", {"start": v(17.64, -16.75) * mm, "end": v(18.12, -17.19) * mm});
            skLineSegment(sketch, "E358", {"start": v(18.12, -17.19) * mm, "end": v(18.7, -17.84) * mm});
            skLineSegment(sketch, "E359", {"start": v(18.7, -17.84) * mm, "end": v(19.39, -18.79) * mm});
            skLineSegment(sketch, "E360", {"start": v(19.39, -18.79) * mm, "end": v(20.14, -20.08) * mm});
            skLineSegment(sketch, "E361", {"start": v(20.14, -20.08) * mm, "end": v(21.02, -21.98) * mm});
            skLineSegment(sketch, "E362", {"start": v(21.02, -21.98) * mm, "end": v(21.9, -24.49) * mm});
            skLineSegment(sketch, "E363", {"start": v(21.9, -24.49) * mm, "end": v(22.44, -26.47) * mm});
            skLineSegment(sketch, "E364", {"start": v(22.44, -26.47) * mm, "end": v(22.86, -28.53) * mm});
            skLineSegment(sketch, "E365", {"start": v(22.86, -28.53) * mm, "end": v(23.07, -28.7) * mm});
            skLineSegment(sketch, "E366", {"start": v(23.07, -28.7) * mm, "end": v(23.3, -28.86) * mm});
            skLineSegment(sketch, "E367", {"start": v(23.3, -28.86) * mm, "end": v(23.67, -29.05) * mm});
            skLineSegment(sketch, "E368", {"start": v(23.67, -29.05) * mm, "end": v(24.41, -29.35) * mm});
            skLineSegment(sketch, "E369", {"start": v(24.41, -29.35) * mm, "end": v(25.24, -29.66) * mm});
            skLineSegment(sketch, "E370", {"start": v(25.24, -29.66) * mm, "end": v(26.08, -30.06) * mm});
            skLineSegment(sketch, "E371", {"start": v(26.08, -30.06) * mm, "end": v(26.13, -29.19) * mm});
            skLineSegment(sketch, "E372", {"start": v(26.13, -29.19) * mm, "end": v(26.1, -28.4) * mm});
            skLineSegment(sketch, "E373", {"start": v(26.1, -28.4) * mm, "end": v(25.98, -27.69) * mm});
            skLineSegment(sketch, "E374", {"start": v(25.98, -27.69) * mm, "end": v(25.8, -27.03) * mm});
            skLineSegment(sketch, "E375", {"start": v(25.8, -27.03) * mm, "end": v(25.51, -26.27) * mm});
            skLineSegment(sketch, "E376", {"start": v(25.51, -26.27) * mm, "end": v(24.1, -23.2) * mm});
            skLineSegment(sketch, "E377", {"start": v(24.1, -23.2) * mm, "end": v(23.98, -22.74) * mm});
            skLineSegment(sketch, "E378", {"start": v(23.98, -22.74) * mm, "end": v(23.88, -22.1) * mm});
            skLineSegment(sketch, "E379", {"start": v(23.88, -22.1) * mm, "end": v(23.83, -21.4) * mm});
            skLineSegment(sketch, "E380", {"start": v(23.83, -21.4) * mm, "end": v(23.87, -20.28) * mm});
            skLineSegment(sketch, "E381", {"start": v(23.87, -20.28) * mm, "end": v(24.02, -17.54) * mm});
            skLineSegment(sketch, "E382", {"start": v(24.02, -17.54) * mm, "end": v(23.99, -16.87) * mm});
            skLineSegment(sketch, "E383", {"start": v(23.99, -16.87) * mm, "end": v(23.88, -16) * mm});
            skLineSegment(sketch, "E384", {"start": v(23.88, -16) * mm, "end": v(21.38, -13.59) * mm});
            skLineSegment(sketch, "E385", {"start": v(21.38, -13.59) * mm, "end": v(20.88, -12.92) * mm});
            skLineSegment(sketch, "E386", {"start": v(20.88, -12.92) * mm, "end": v(20.62, -12.5) * mm});
            skLineSegment(sketch, "E387", {"start": v(20.62, -12.5) * mm, "end": v(20.42, -12.08) * mm});
            skLineSegment(sketch, "E388", {"start": v(20.42, -12.08) * mm, "end": v(20.26, -11.64) * mm});
            skLineSegment(sketch, "E389", {"start": v(20.26, -11.64) * mm, "end": v(20.2, -11.34) * mm});
            skLineSegment(sketch, "E390", {"start": v(20.2, -11.34) * mm, "end": v(20.15, -11.03) * mm});
            skLineSegment(sketch, "E391", {"start": v(20.15, -11.03) * mm, "end": v(20.15, -10.71) * mm});
            skLineSegment(sketch, "E392", {"start": v(20.15, -10.71) * mm, "end": v(20.17, -10.4) * mm});
            skLineSegment(sketch, "E393", {"start": v(20.17, -10.4) * mm, "end": v(20.24, -10.07) * mm});
            skLineSegment(sketch, "E394", {"start": v(20.24, -10.07) * mm, "end": v(20.34, -9.74) * mm});
            skLineSegment(sketch, "E395", {"start": v(20.34, -9.74) * mm, "end": v(20.49, -9.4) * mm});
            skLineSegment(sketch, "E396", {"start": v(20.49, -9.4) * mm, "end": v(20.67, -9.45) * mm});
            skLineSegment(sketch, "E397", {"start": v(20.67, -9.45) * mm, "end": v(20.85, -9.52) * mm});
            skLineSegment(sketch, "E398", {"start": v(20.85, -9.52) * mm, "end": v(21.01, -9.62) * mm});
            skLineSegment(sketch, "E399", {"start": v(21.01, -9.62) * mm, "end": v(21.17, -9.73) * mm});
            skLineSegment(sketch, "E400", {"start": v(21.17, -9.73) * mm, "end": v(21.4, -9.94) * mm});
            skLineSegment(sketch, "E401", {"start": v(21.4, -9.94) * mm, "end": v(21.6, -10.18) * mm});
            skLineSegment(sketch, "E402", {"start": v(21.6, -10.18) * mm, "end": v(21.91, -10.63) * mm});
            skLineSegment(sketch, "E403", {"start": v(21.91, -10.63) * mm, "end": v(22.9, -12.27) * mm});
            skLineSegment(sketch, "E404", {"start": v(22.9, -12.27) * mm, "end": v(23, -12.39) * mm});
            skLineSegment(sketch, "E405", {"start": v(23, -12.39) * mm, "end": v(23.1, -12.48) * mm});
            skLineSegment(sketch, "E406", {"start": v(23.1, -12.48) * mm, "end": v(23.2, -12.56) * mm});
            skLineSegment(sketch, "E407", {"start": v(23.2, -12.56) * mm, "end": v(23.26, -12.59) * mm});
            skLineSegment(sketch, "E408", {"start": v(23.26, -12.59) * mm, "end": v(23.32, -12.6) * mm});
            skLineSegment(sketch, "E409", {"start": v(23.32, -12.6) * mm, "end": v(23.37, -12.62) * mm});
            skLineSegment(sketch, "E410", {"start": v(23.37, -12.62) * mm, "end": v(23.42, -12.63) * mm});
            skLineSegment(sketch, "E411", {"start": v(23.42, -12.63) * mm, "end": v(23.48, -12.62) * mm});
            skLineSegment(sketch, "E412", {"start": v(23.48, -12.62) * mm, "end": v(23.54, -12.62) * mm});
            skLineSegment(sketch, "E413", {"start": v(23.54, -12.62) * mm, "end": v(23.5, -12.61) * mm});
            skLineSegment(sketch, "E414", {"start": v(23.5, -12.61) * mm, "end": v(23.48, -12.6) * mm});
            skLineSegment(sketch, "E415", {"start": v(23.48, -12.6) * mm, "end": v(23.46, -12.59) * mm});
            skLineSegment(sketch, "E416", {"start": v(23.46, -12.59) * mm, "end": v(23.44, -12.58) * mm});
            skLineSegment(sketch, "E417", {"start": v(23.44, -12.58) * mm, "end": v(23.43, -12.56) * mm});
            skLineSegment(sketch, "E418", {"start": v(23.43, -12.56) * mm, "end": v(23.41, -12.54) * mm});
            skLineSegment(sketch, "E419", {"start": v(23.41, -12.54) * mm, "end": v(23.4, -12.52) * mm});
            skLineSegment(sketch, "E420", {"start": v(23.4, -12.52) * mm, "end": v(23.39, -12.5) * mm});
            skLineSegment(sketch, "E421", {"start": v(23.39, -12.5) * mm, "end": v(23.38, -12.45) * mm});
            skLineSegment(sketch, "E422", {"start": v(23.38, -12.45) * mm, "end": v(23.37, -12.41) * mm});
            skLineSegment(sketch, "E423", {"start": v(23.37, -12.41) * mm, "end": v(23.36, -12.18) * mm});
            skLineSegment(sketch, "E424", {"start": v(23.36, -12.18) * mm, "end": v(23.37, -11.94) * mm});
            skLineSegment(sketch, "E425", {"start": v(23.37, -11.94) * mm, "end": v(23.45, -12.06) * mm});
            skLineSegment(sketch, "E426", {"start": v(23.45, -12.06) * mm, "end": v(23.54, -12.17) * mm});
            skLineSegment(sketch, "E427", {"start": v(23.54, -12.17) * mm, "end": v(23.64, -12.26) * mm});
            skLineSegment(sketch, "E428", {"start": v(23.64, -12.26) * mm, "end": v(23.75, -12.34) * mm});
            skLineSegment(sketch, "E429", {"start": v(23.75, -12.34) * mm, "end": v(23.9, -12.44) * mm});
            skLineSegment(sketch, "E430", {"start": v(23.9, -12.44) * mm, "end": v(24.08, -12.53) * mm});
            skLineSegment(sketch, "E431", {"start": v(24.08, -12.53) * mm, "end": v(24.8, -12.75) * mm});
            skLineSegment(sketch, "E432", {"start": v(24.8, -12.75) * mm, "end": v(25.57, -12.95) * mm});
            skLineSegment(sketch, "E433", {"start": v(25.57, -12.95) * mm, "end": v(27.26, -13.4) * mm});
            skLineSegment(sketch, "E434", {"start": v(27.26, -13.4) * mm, "end": v(28.6, -13.6) * mm});
            skLineSegment(sketch, "E435", {"start": v(28.6, -13.6) * mm, "end": v(29.88, -13.68) * mm});
            skLineSegment(sketch, "E436", {"start": v(29.88, -13.68) * mm, "end": v(30.87, -13.65) * mm});
            skLineSegment(sketch, "E437", {"start": v(30.87, -13.65) * mm, "end": v(31.81, -13.53) * mm});
            skLineSegment(sketch, "E438", {"start": v(31.81, -13.53) * mm, "end": v(32.72, -13.33) * mm});
            skLineSegment(sketch, "E439", {"start": v(32.72, -13.33) * mm, "end": v(33.6, -13.04) * mm});
            skLineSegment(sketch, "E440", {"start": v(33.6, -13.04) * mm, "end": v(34.43, -12.67) * mm});
            skLineSegment(sketch, "E441", {"start": v(34.43, -12.67) * mm, "end": v(35.23, -12.22) * mm});
            skLineSegment(sketch, "E442", {"start": v(35.23, -12.22) * mm, "end": v(36, -11.7) * mm});
            skLineSegment(sketch, "E443", {"start": v(36, -11.7) * mm, "end": v(36.55, -11.25) * mm});
            skLineSegment(sketch, "E444", {"start": v(36.55, -11.25) * mm, "end": v(37.08, -10.75) * mm});
            skLineSegment(sketch, "E445", {"start": v(37.08, -10.75) * mm, "end": v(37.25, -10.61) * mm});
            skLineSegment(sketch, "E446", {"start": v(37.25, -10.61) * mm, "end": v(38.03, -9.98) * mm});
            skLineSegment(sketch, "E447", {"start": v(38.03, -9.98) * mm, "end": v(38.15, -9.84) * mm});
            skLineSegment(sketch, "E448", {"start": v(38.15, -9.84) * mm, "end": v(38.23, -9.74) * mm});
            skLineSegment(sketch, "E449", {"start": v(38.23, -9.74) * mm, "end": v(38.27, -9.67) * mm});
            skLineSegment(sketch, "E450", {"start": v(38.27, -9.67) * mm, "end": v(38.3, -9.6) * mm});
            skLineSegment(sketch, "E451", {"start": v(38.3, -9.6) * mm, "end": v(38.33, -9.52) * mm});
            skLineSegment(sketch, "E452", {"start": v(38.33, -9.52) * mm, "end": v(38.34, -9.44) * mm});
            skLineSegment(sketch, "E453", {"start": v(38.34, -9.44) * mm, "end": v(38.35, -9.36) * mm});
            skLineSegment(sketch, "E454", {"start": v(38.35, -9.36) * mm, "end": v(38.34, -9.28) * mm});
            skLineSegment(sketch, "E455", {"start": v(38.34, -9.28) * mm, "end": v(38.32, -9.2) * mm});
            skLineSegment(sketch, "E456", {"start": v(38.32, -9.2) * mm, "end": v(38.3, -9.15) * mm});
            skLineSegment(sketch, "E457", {"start": v(38.3, -9.15) * mm, "end": v(38.27, -9.06) * mm});
            skLineSegment(sketch, "E458", {"start": v(38.27, -9.06) * mm, "end": v(36.5, -9.6) * mm});
            skLineSegment(sketch, "E459", {"start": v(36.5, -9.6) * mm, "end": v(35.4, -9.8) * mm});
            skLineSegment(sketch, "E460", {"start": v(35.4, -9.8) * mm, "end": v(34.34, -9.89) * mm});
            skLineSegment(sketch, "E461", {"start": v(34.34, -9.89) * mm, "end": v(33.35, -9.86) * mm});
            skLineSegment(sketch, "E462", {"start": v(33.35, -9.86) * mm, "end": v(32.4, -9.73) * mm});
            skLineSegment(sketch, "E463", {"start": v(32.4, -9.73) * mm, "end": v(31.5, -9.5) * mm});
            skLineSegment(sketch, "E464", {"start": v(31.5, -9.5) * mm, "end": v(30.66, -9.2) * mm});
            skLineSegment(sketch, "E465", {"start": v(30.66, -9.2) * mm, "end": v(29.84, -8.8) * mm});
            skLineSegment(sketch, "E466", {"start": v(29.84, -8.8) * mm, "end": v(28.7, -8.1) * mm});
            skLineSegment(sketch, "E467", {"start": v(28.7, -8.1) * mm, "end": v(27.62, -7.25) * mm});
            skLineSegment(sketch, "E468", {"start": v(27.62, -7.25) * mm, "end": v(26.28, -5.97) * mm});
            skLineSegment(sketch, "E469", {"start": v(26.28, -5.97) * mm, "end": v(23.84, -3.1) * mm});
            skLineSegment(sketch, "E470", {"start": v(23.84, -3.1) * mm, "end": v(21.82, -0.6) * mm});
            skLineSegment(sketch, "E471", {"start": v(21.82, -0.6) * mm, "end": v(19.47, 1.78) * mm});
            skLineSegment(sketch, "E472", {"start": v(19.47, 1.78) * mm, "end": v(18.49, 2.5) * mm});
            skLineSegment(sketch, "E473", {"start": v(18.49, 2.5) * mm, "end": v(17.19, 3.3) * mm});
            skLineSegment(sketch, "E474", {"start": v(17.19, 3.3) * mm, "end": v(15.56, 4.08) * mm});
            skLineSegment(sketch, "E475", {"start": v(15.56, 4.08) * mm, "end": v(12.7, 5.14) * mm});
            skLineSegment(sketch, "E476", {"start": v(12.7, 5.14) * mm, "end": v(9.12, 6.26) * mm});
            skLineSegment(sketch, "E477", {"start": v(9.12, 6.26) * mm, "end": v(5.25, 7.7) * mm});
            skLineSegment(sketch, "E478", {"start": v(5.25, 7.7) * mm, "end": v(1.04, 9.8) * mm});
            skLineSegment(sketch, "E479", {"start": v(1.04, 9.8) * mm, "end": v(-2.15, 11.8) * mm});
            skLineSegment(sketch, "E480", {"start": v(-2.15, 11.8) * mm, "end": v(-4.44, 13.56) * mm});
            skLineSegment(sketch, "E481", {"start": v(-4.44, 13.56) * mm, "end": v(-6.24, 15.24) * mm});
            skLineSegment(sketch, "E482", {"start": v(-6.24, 15.24) * mm, "end": v(-7.86, 17.07) * mm});
            skLineSegment(sketch, "E483", {"start": v(-7.86, 17.07) * mm, "end": v(-9.07, 18.74) * mm});
            skLineSegment(sketch, "E484", {"start": v(-9.07, 18.74) * mm, "end": v(-9.73, 19.8) * mm});
            skLineSegment(sketch, "E485", {"start": v(-9.73, 19.8) * mm, "end": v(-10.33, 20.91) * mm});
            skLineSegment(sketch, "E486", {"start": v(-10.33, 20.91) * mm, "end": v(-10.1, 20.9) * mm});
            skLineSegment(sketch, "E487", {"start": v(-10.1, 20.9) * mm, "end": v(-9.88, 20.9) * mm});
            skLineSegment(sketch, "E488", {"start": v(-9.88, 20.9) * mm, "end": v(-9.68, 20.93) * mm});
            skLineSegment(sketch, "E489", {"start": v(-9.68, 20.93) * mm, "end": v(-9.47, 20.99) * mm});
            skLineSegment(sketch, "E490", {"start": v(-9.47, 20.99) * mm, "end": v(-9.14, 21.1) * mm});
            skLineSegment(sketch, "E491", {"start": v(-9.14, 21.1) * mm, "end": v(-8.8, 21.25) * mm});
            skLineSegment(sketch, "E492", {"start": v(-8.8, 21.25) * mm, "end": v(-8.82, 21.34) * mm});
            skLineSegment(sketch, "E493", {"start": v(-8.82, 21.34) * mm, "end": v(-8.84, 21.43) * mm});
            skLineSegment(sketch, "E494", {"start": v(-8.84, 21.43) * mm, "end": v(-8.88, 21.52) * mm});
            skLineSegment(sketch, "E495", {"start": v(-8.88, 21.52) * mm, "end": v(-8.93, 21.61) * mm});
            skLineSegment(sketch, "E496", {"start": v(-8.93, 21.61) * mm, "end": v(-9.02, 21.75) * mm});
            skLineSegment(sketch, "E497", {"start": v(-9.02, 21.75) * mm, "end": v(-9.17, 21.93) * mm});
            skLineSegment(sketch, "E498", {"start": v(-9.17, 21.93) * mm, "end": v(-10.07, 22.69) * mm});
            skLineSegment(sketch, "E499", {"start": v(-10.07, 22.69) * mm, "end": v(-11, 23.45) * mm});
            skLineSegment(sketch, "E500", {"start": v(-11, 23.45) * mm, "end": v(-11.09, 24.12) * mm});
            skLineSegment(sketch, "E501", {"start": v(-11.09, 24.12) * mm, "end": v(-11.23, 24.74) * mm});
            skLineSegment(sketch, "E502", {"start": v(-11.23, 24.74) * mm, "end": v(-11.43, 25.31) * mm});
            skLineSegment(sketch, "E503", {"start": v(-11.43, 25.31) * mm, "end": v(-11.69, 25.86) * mm});
            skLineSegment(sketch, "E504", {"start": v(-11.69, 25.86) * mm, "end": v(-12.1, 26.53) * mm});
            skLineSegment(sketch, "E505", {"start": v(-12.1, 26.53) * mm, "end": v(-12.7, 27.32) * mm});
            skLineSegment(sketch, "E506", {"start": v(-12.7, 27.32) * mm, "end": v(-15.9, 30.89) * mm});
            skLineSegment(sketch, "E507", {"start": v(-15.9, 30.89) * mm, "end": v(-16.13, 31.22) * mm});
            skLineSegment(sketch, "E508", {"start": v(-16.13, 31.22) * mm, "end": v(-16.43, 31.75) * mm});
            skLineSegment(sketch, "E509", {"start": v(-16.43, 31.75) * mm, "end": v(-16.6, 32.12) * mm});
            skLineSegment(sketch, "E510", {"start": v(-16.6, 32.12) * mm, "end": v(-17.4, 34.25) * mm});
            skLineSegment(sketch, "E511", {"start": v(-17.4, 34.25) * mm, "end": v(-17.56, 34.54) * mm});
            skLineSegment(sketch, "E512", {"start": v(-17.56, 34.54) * mm, "end": v(-17.7, 34.72) * mm});
            skLineSegment(sketch, "E513", {"start": v(-17.7, 34.72) * mm, "end": v(-17.8, 34.83) * mm});
            skLineSegment(sketch, "E514", {"start": v(-17.8, 34.83) * mm, "end": v(-17.9, 34.92) * mm});
            skLineSegment(sketch, "E515", {"start": v(-17.9, 34.92) * mm, "end": v(-18, 35) * mm});
            skLineSegment(sketch, "E516", {"start": v(-18, 35) * mm, "end": v(-18.13, 35.06) * mm});
            skLineSegment(sketch, "E517", {"start": v(-18.13, 35.06) * mm, "end": v(-18.25, 35.1) * mm});
            skLineSegment(sketch, "E518", {"start": v(-18.25, 35.1) * mm, "end": v(-18.32, 35.12) * mm});
            skLineSegment(sketch, "E519", {"start": v(-18.32, 35.12) * mm, "end": v(-18.46, 35.14) * mm});
            skLineSegment(sketch, "E520", {"start": v(-18.46, 35.14) * mm, "end": v(-18.6, 35.13) * mm});
            skLineSegment(sketch, "E521", {"start": v(-18.6, 35.13) * mm, "end": v(-18.72, 35.11) * mm});
            skLineSegment(sketch, "E522", {"start": v(-18.72, 35.11) * mm, "end": v(-18.85, 35.07) * mm});
            skLineSegment(sketch, "E523", {"start": v(-18.85, 35.07) * mm, "end": v(-18.96, 35.02) * mm});
            skLineSegment(sketch, "E524", {"start": v(-18.96, 35.02) * mm, "end": v(-19.07, 34.95) * mm});
            skLineSegment(sketch, "E525", {"start": v(-19.07, 34.95) * mm, "end": v(-19.17, 34.86) * mm});
            skLineSegment(sketch, "E526", {"start": v(-19.17, 34.86) * mm, "end": v(-19.26, 34.77) * mm});
            skLineSegment(sketch, "E527", {"start": v(-19.26, 34.77) * mm, "end": v(-19.4, 34.6) * mm});
            skLineSegment(sketch, "E528", {"start": v(-19.4, 34.6) * mm, "end": v(-19.5, 34.43) * mm});
            skLineSegment(sketch, "E529", {"start": v(-19.5, 34.43) * mm, "end": v(-19.64, 34.16) * mm});
            skLineSegment(sketch, "E530", {"start": v(-19.64, 34.16) * mm, "end": v(-19.8, 33.74) * mm});
            skLineSegment(sketch, "E531", {"start": v(-19.8, 33.74) * mm, "end": v(-20.01, 33.02) * mm});
            skLineSegment(sketch, "E532", {"start": v(-20.01, 33.02) * mm, "end": v(-20.15, 32.43) * mm});
            skLineSegment(sketch, "E533", {"start": v(-20.15, 32.43) * mm, "end": v(-20.54, 32.46) * mm});
            skLineSegment(sketch, "E534", {"start": v(-20.54, 32.46) * mm, "end": v(-20.78, 32.45) * mm});
            skLineSegment(sketch, "E535", {"start": v(-20.78, 32.45) * mm, "end": v(-20.97, 32.43) * mm});
            skLineSegment(sketch, "E536", {"start": v(-20.97, 32.43) * mm, "end": v(-21.1, 32.4) * mm});
            skLineSegment(sketch, "E537", {"start": v(-21.1, 32.4) * mm, "end": v(-21.22, 32.36) * mm});
            skLineSegment(sketch, "E538", {"start": v(-21.22, 32.36) * mm, "end": v(-21.3, 32.32) * mm});
            skLineSegment(sketch, "E539", {"start": v(-21.3, 32.32) * mm, "end": v(-21.39, 32.28) * mm});
            skLineSegment(sketch, "E540", {"start": v(-21.39, 32.28) * mm, "end": v(-21.46, 32.23) * mm});
            skLineSegment(sketch, "E541", {"start": v(-21.46, 32.23) * mm, "end": v(-21.52, 32.17) * mm});
            skLineSegment(sketch, "E542", {"start": v(-21.52, 32.17) * mm, "end": v(-21.58, 32.1) * mm});
            skLineSegment(sketch, "E543", {"start": v(-21.58, 32.1) * mm, "end": v(-21.62, 32.03) * mm});
            skLineSegment(sketch, "E544", {"start": v(-21.62, 32.03) * mm, "end": v(-21.65, 31.98) * mm});
            skLineSegment(sketch, "E545", {"start": v(-21.65, 31.98) * mm, "end": v(-21.67, 31.92) * mm});
            skLineSegment(sketch, "E546", {"start": v(-21.67, 31.92) * mm, "end": v(-21.45, 31.38) * mm});
            skLineSegment(sketch, "E547", {"start": v(-21.45, 31.38) * mm, "end": v(-21.29, 30.8) * mm});
            skLineSegment(sketch, "E548", {"start": v(-21.29, 30.8) * mm, "end": v(-21.14, 29.98) * mm});
            skLineSegment(sketch, "E549", {"start": v(-21.14, 29.98) * mm, "end": v(-21.05, 28.89) * mm});
            skLineSegment(sketch, "E550", {"start": v(-21.05, 28.89) * mm, "end": v(-21.08, 27.06) * mm});
            skLineSegment(sketch, "E551", {"start": v(-21.08, 27.06) * mm, "end": v(-21.3, 24.11) * mm});
            skLineSegment(sketch, "E552", {"start": v(-21.3, 24.11) * mm, "end": v(-21.34, 21.42) * mm});
            skLineSegment(sketch, "E553", {"start": v(-21.34, 21.42) * mm, "end": v(-21.4, 21.4) * mm});
            skLineSegment(sketch, "E554", {"start": v(-21.4, 21.4) * mm, "end": v(-21.47, 21.4) * mm});
            skLineSegment(sketch, "E555", {"start": v(-21.47, 21.4) * mm, "end": v(-21.54, 21.4) * mm});
            skLineSegment(sketch, "E556", {"start": v(-21.54, 21.4) * mm, "end": v(-21.64, 21.4) * mm});
            skLineSegment(sketch, "E557", {"start": v(-21.64, 21.4) * mm, "end": v(-21.78, 21.43) * mm});
            skLineSegment(sketch, "E558", {"start": v(-21.78, 21.43) * mm, "end": v(-22.05, 21.51) * mm});
            skLineSegment(sketch, "E559", {"start": v(-22.05, 21.51) * mm, "end": v(-22.33, 21.6) * mm});
            skLineSegment(sketch, "E560", {"start": v(-22.33, 21.6) * mm, "end": v(-22.42, 21.61) * mm});
            skLineSegment(sketch, "E561", {"start": v(-22.42, 21.61) * mm, "end": v(-22.48, 21.62) * mm});
            skLineSegment(sketch, "E562", {"start": v(-22.48, 21.62) * mm, "end": v(-22.53, 21.62) * mm});
            skLineSegment(sketch, "E563", {"start": v(-22.53, 21.62) * mm, "end": v(-22.59, 21.6) * mm});
            skLineSegment(sketch, "E564", {"start": v(-22.59, 21.6) * mm, "end": v(-22.64, 21.6) * mm});
            skLineSegment(sketch, "E565", {"start": v(-22.64, 21.6) * mm, "end": v(-22.7, 21.57) * mm});
            skLineSegment(sketch, "E566", {"start": v(-22.7, 21.57) * mm, "end": v(-22.74, 21.54) * mm});
            skLineSegment(sketch, "E567", {"start": v(-22.74, 21.54) * mm, "end": v(-22.8, 21.5) * mm});
            skLineSegment(sketch, "E568", {"start": v(-22.8, 21.5) * mm, "end": v(-22.81, 21.48) * mm});
            skLineSegment(sketch, "E569", {"start": v(-22.81, 21.48) * mm, "end": v(-22.86, 21.42) * mm});
            skLineSegment(sketch, "E570", {"start": v(-22.86, 21.42) * mm, "end": v(-22.18, 20.97) * mm});
            skLineSegment(sketch, "E571", {"start": v(-22.18, 20.97) * mm, "end": v(-22.03, 20.83) * mm});
            skLineSegment(sketch, "E572", {"start": v(-22.03, 20.83) * mm, "end": v(-21.94, 20.73) * mm});
            skLineSegment(sketch, "E573", {"start": v(-21.94, 20.73) * mm, "end": v(-21.85, 20.63) * mm});
            skLineSegment(sketch, "E574", {"start": v(-21.85, 20.63) * mm, "end": v(-21.78, 20.5) * mm});
            skLineSegment(sketch, "E575", {"start": v(-21.78, 20.5) * mm, "end": v(-21.72, 20.38) * mm});
            skLineSegment(sketch, "E576", {"start": v(-21.72, 20.38) * mm, "end": v(-21.67, 20.23) * mm});
            skLineSegment(sketch, "E577", {"start": v(-21.67, 20.23) * mm, "end": v(-22.02, 20.1) * mm});
            skLineSegment(sketch, "E578", {"start": v(-22.02, 20.1) * mm, "end": v(-22.14, 20.03) * mm});
            skLineSegment(sketch, "E579", {"start": v(-22.14, 20.03) * mm, "end": v(-22.23, 19.96) * mm});
            skLineSegment(sketch, "E580", {"start": v(-22.23, 19.96) * mm, "end": v(-22.28, 19.92) * mm});
            skLineSegment(sketch, "E581", {"start": v(-22.28, 19.92) * mm, "end": v(-22.3, 19.88) * mm});
            skLineSegment(sketch, "E582", {"start": v(-22.3, 19.88) * mm, "end": v(-22.32, 19.86) * mm});
            skLineSegment(sketch, "E583", {"start": v(-22.32, 19.86) * mm, "end": v(-22.33, 19.84) * mm});
            skLineSegment(sketch, "E584", {"start": v(-22.33, 19.84) * mm, "end": v(-22.34, 19.82) * mm});
            skLineSegment(sketch, "E585", {"start": v(-22.34, 19.82) * mm, "end": v(-22.35, 19.8) * mm});
            skLineSegment(sketch, "E586", {"start": v(-22.35, 19.8) * mm, "end": v(-22.35, 19.77) * mm});
            skLineSegment(sketch, "E587", {"start": v(-22.35, 19.77) * mm, "end": v(-22.35, 19.75) * mm});
            skLineSegment(sketch, "E588", {"start": v(-22.35, 19.75) * mm, "end": v(-22.35, 19.73) * mm});
            skLineSegment(sketch, "E589", {"start": v(-22.35, 19.73) * mm, "end": v(-22.34, 19.69) * mm});
            skLineSegment(sketch, "E590", {"start": v(-22.34, 19.69) * mm, "end": v(-22.32, 19.64) * mm});
            skLineSegment(sketch, "E591", {"start": v(-22.32, 19.64) * mm, "end": v(-22.3, 19.6) * mm});
            skLineSegment(sketch, "E592", {"start": v(-22.3, 19.6) * mm, "end": v(-22.24, 19.5) * mm});
            skLineSegment(sketch, "E593", {"start": v(-22.24, 19.5) * mm, "end": v(-22.06, 19.24) * mm});
            skLineSegment(sketch, "E594", {"start": v(-22.06, 19.24) * mm, "end": v(-21.84, 18.88) * mm});
            skLineSegment(sketch, "E595", {"start": v(-21.84, 18.88) * mm, "end": v(-22.25, 16.8) * mm});
            skLineSegment(sketch, "E596", {"start": v(-22.25, 16.8) * mm, "end": v(-22.46, 14.64) * mm});
            skLineSegment(sketch, "E597", {"start": v(-22.46, 14.64) * mm, "end": v(-22.48, 12.37) * mm});
            skLineSegment(sketch, "E598", {"start": v(-22.48, 12.37) * mm, "end": v(-22.37, 10.89) * mm});
            skLineSegment(sketch, "E599", {"start": v(-22.37, 10.89) * mm, "end": v(-22.18, 9.23) * mm});
            skLineSegment(sketch, "E600", {"start": v(-22.18, 9.23) * mm, "end": v(-21.89, 7.6) * mm});
            skLineSegment(sketch, "E601", {"start": v(-21.89, 7.6) * mm, "end": v(-21.32, 5.64) * mm});
            skLineSegment(sketch, "E602", {"start": v(-21.32, 5.64) * mm, "end": v(-19.13, -0.84) * mm});
            skLineSegment(sketch, "E603", {"start": v(-19.13, -0.84) * mm, "end": v(-18.93, -1.87) * mm});
            skLineSegment(sketch, "E604", {"start": v(-18.93, -1.87) * mm, "end": v(-18.8, -2.96) * mm});
            skLineSegment(sketch, "E605", {"start": v(-18.8, -2.96) * mm, "end": v(-18.6, -1.74) * mm});
            skLineSegment(sketch, "E606", {"start": v(-18.6, -1.74) * mm, "end": v(-18.5, -1.42) * mm});
            skLineSegment(sketch, "E607", {"start": v(-18.5, -1.42) * mm, "end": v(-18.43, -1.23) * mm});
            skLineSegment(sketch, "E608", {"start": v(-18.43, -1.23) * mm, "end": v(-18.36, -1.1) * mm});
            skLineSegment(sketch, "E609", {"start": v(-18.36, -1.1) * mm, "end": v(-18.28, -0.98) * mm});
            skLineSegment(sketch, "E610", {"start": v(-18.28, -0.98) * mm, "end": v(-18.19, -0.87) * mm});
            skLineSegment(sketch, "E611", {"start": v(-18.19, -0.87) * mm, "end": v(-18.08, -0.77) * mm});
            skLineSegment(sketch, "E612", {"start": v(-18.08, -0.77) * mm, "end": v(-18, -0.7) * mm});
            skLineSegment(sketch, "E613", {"start": v(-18, -0.7) * mm, "end": v(-17.92, -0.66) * mm});
            skLineSegment(sketch, "E614", {"start": v(-17.92, -0.66) * mm, "end": v(-17.88, -0.63) * mm});
            skLineSegment(sketch, "E615", {"start": v(-17.88, -0.63) * mm, "end": v(-17.78, -0.6) * mm});
            skLineSegment(sketch, "E616", {"start": v(-17.78, -0.6) * mm, "end": v(-17.74, -0.66) * mm});
            skLineSegment(sketch, "E617", {"start": v(-17.74, -0.66) * mm, "end": v(-17.7, -0.74) * mm});
            skLineSegment(sketch, "E618", {"start": v(-17.7, -0.74) * mm, "end": v(-17.67, -0.86) * mm});
            skLineSegment(sketch, "E619", {"start": v(-17.67, -0.86) * mm, "end": v(-17.65, -1) * mm});
            skLineSegment(sketch, "E620", {"start": v(-17.65, -1) * mm, "end": v(-17.62, -1.25) * mm});
            skLineSegment(sketch, "E621", {"start": v(-17.62, -1.25) * mm, "end": v(-17.6, -2.52) * mm});
            skLineSegment(sketch, "E622", {"start": v(-17.6, -2.52) * mm, "end": v(-17.56, -2.7) * mm});
            skLineSegment(sketch, "E623", {"start": v(-17.56, -2.7) * mm, "end": v(-17.52, -2.82) * mm});
            skLineSegment(sketch, "E624", {"start": v(-17.52, -2.82) * mm, "end": v(-17.48, -2.9) * mm});
            skLineSegment(sketch, "E625", {"start": v(-17.48, -2.9) * mm, "end": v(-17.44, -2.96) * mm});
            skLineSegment(sketch, "E626", {"start": v(-17.44, -2.96) * mm, "end": v(-17.42, -2.98) * mm});
            skLineSegment(sketch, "E627", {"start": v(-17.42, -2.98) * mm, "end": v(-17.4, -2.99) * mm});
            skLineSegment(sketch, "E628", {"start": v(-17.4, -2.99) * mm, "end": v(-17.37, -3) * mm});
            skLineSegment(sketch, "E629", {"start": v(-17.37, -3) * mm, "end": v(-17.35, -3) * mm});
            skLineSegment(sketch, "E630", {"start": v(-17.35, -3) * mm, "end": v(-17.33, -3) * mm});
            skLineSegment(sketch, "E631", {"start": v(-17.33, -3) * mm, "end": v(-17.3, -2.99) * mm});
            skLineSegment(sketch, "E632", {"start": v(-17.3, -2.99) * mm, "end": v(-17.29, -2.98) * mm});
            skLineSegment(sketch, "E633", {"start": v(-17.29, -2.98) * mm, "end": v(-17.26, -2.97) * mm});
            skLineSegment(sketch, "E634", {"start": v(-17.26, -2.97) * mm, "end": v(-17.24, -2.95) * mm});
            skLineSegment(sketch, "E635", {"start": v(-17.24, -2.95) * mm, "end": v(-17.2, -2.9) * mm});
            skLineSegment(sketch, "E636", {"start": v(-17.2, -2.9) * mm, "end": v(-17.13, -2.83) * mm});
            skLineSegment(sketch, "E637", {"start": v(-17.13, -2.83) * mm, "end": v(-16.76, -2.32) * mm});
            skLineSegment(sketch, "E638", {"start": v(-16.76, -2.32) * mm, "end": v(-16.67, -2.23) * mm});
            skLineSegment(sketch, "E639", {"start": v(-16.67, -2.23) * mm, "end": v(-16.6, -2.18) * mm});
            skLineSegment(sketch, "E640", {"start": v(-16.6, -2.18) * mm, "end": v(-16.54, -2.14) * mm});
            skLineSegment(sketch, "E641", {"start": v(-16.54, -2.14) * mm, "end": v(-16.46, -2.12) * mm});
            skLineSegment(sketch, "E642", {"start": v(-16.46, -2.12) * mm, "end": v(-16.42, -2.1) * mm});
            skLineSegment(sketch, "E643", {"start": v(-16.42, -2.1) * mm, "end": v(-16.39, -2.1) * mm});
            skLineSegment(sketch, "E644", {"start": v(-16.39, -2.1) * mm, "end": v(-16.34, -2.1) * mm});
            skLineSegment(sketch, "E645", {"start": v(-16.34, -2.1) * mm, "end": v(-16.3, -2.1) * mm});
            skLineSegment(sketch, "E646", {"start": v(-16.3, -2.1) * mm, "end": v(-16.26, -2.1) * mm});
            skLineSegment(sketch, "E647", {"start": v(-16.26, -2.1) * mm, "end": v(-16.21, -2.12) * mm});
            skLineSegment(sketch, "E648", {"start": v(-16.21, -2.12) * mm, "end": v(-16.12, -2.16) * mm});
            skLineSegment(sketch, "E649", {"start": v(-16.12, -2.16) * mm, "end": v(-16.02, -2.21) * mm});
            skLineSegment(sketch, "E650", {"start": v(-16.02, -2.21) * mm, "end": v(-15.92, -2.29) * mm});
            skLineSegment(sketch, "E651", {"start": v(-15.92, -2.29) * mm, "end": v(-16.03, -2.73) * mm});
            skLineSegment(sketch, "E652", {"start": v(-16.03, -2.73) * mm, "end": v(-16.09, -3.16) * mm});
            skLineSegment(sketch, "E653", {"start": v(-16.09, -3.16) * mm, "end": v(-16.1, -3.55) * mm});
            skLineSegment(sketch, "E654", {"start": v(-16.1, -3.55) * mm, "end": v(-16.06, -3.93) * mm});
            skLineSegment(sketch, "E655", {"start": v(-16.06, -3.93) * mm, "end": v(-15.99, -4.28) * mm});
            skLineSegment(sketch, "E656", {"start": v(-15.99, -4.28) * mm, "end": v(-15.88, -4.61) * mm});
            skLineSegment(sketch, "E657", {"start": v(-15.88, -4.61) * mm, "end": v(-15.7, -5.03) * mm});
            skLineSegment(sketch, "E658", {"start": v(-15.7, -5.03) * mm, "end": v(-15.41, -5.52) * mm});
            skLineSegment(sketch, "E659", {"start": v(-15.41, -5.52) * mm, "end": v(-14.7, -6.5) * mm});
            skLineSegment(sketch, "E660", {"start": v(-14.7, -6.5) * mm, "end": v(-14.06, -7.54) * mm});
            skLineSegment(sketch, "E661", {"start": v(-14.06, -7.54) * mm, "end": v(-13.87, -8) * mm});
            skLineSegment(sketch, "E662", {"start": v(-13.87, -8) * mm, "end": v(-13.73, -8.5) * mm});
            skLineSegment(sketch, "E663", {"start": v(-13.73, -8.5) * mm, "end": v(-13.6, -9.16) * mm});
            skLineSegment(sketch, "E664", {"start": v(-13.6, -9.16) * mm, "end": v(-13.54, -10.02) * mm});
            skLineSegment(sketch, "E665", {"start": v(-13.54, -10.02) * mm, "end": v(-13.56, -11.29) * mm});
            skLineSegment(sketch, "E666", {"start": v(-13.56, -11.29) * mm, "end": v(-13.8, -14.03) * mm});
            skLineSegment(sketch, "E667", {"start": v(-13.8, -14.03) * mm, "end": v(-13.89, -17.02) * mm});
            skLineSegment(sketch, "E668", {"start": v(-13.89, -17.02) * mm, "end": v(-15.12, -16.74) * mm});
            skLineSegment(sketch, "E669", {"start": v(-15.12, -16.74) * mm, "end": v(-16.25, -16.62) * mm});
            skLineSegment(sketch, "E670", {"start": v(-16.25, -16.62) * mm, "end": v(-16.95, -16.62) * mm});
            skLineSegment(sketch, "E671", {"start": v(-16.95, -16.62) * mm, "end": v(-17.6, -16.68) * mm});
            skLineSegment(sketch, "E672", {"start": v(-17.6, -16.68) * mm, "end": v(-18.53, -16.87) * mm});
            skLineSegment(sketch, "E673", {"start": v(-18.53, -16.87) * mm, "end": v(-19.4, -17.16) * mm});
            skLineSegment(sketch, "E674", {"start": v(-19.4, -17.16) * mm, "end": v(-20.2, -17.52) * mm});
            skLineSegment(sketch, "E675", {"start": v(-20.2, -17.52) * mm, "end": v(-21.5, -18.24) * mm});
            skLineSegment(sketch, "E676", {"start": v(-21.5, -18.24) * mm, "end": v(-24.57, -20.09) * mm});
            skLineSegment(sketch, "E677", {"start": v(-24.57, -20.09) * mm, "end": v(-25.71, -20.58) * mm});
            skLineSegment(sketch, "E678", {"start": v(-25.71, -20.58) * mm, "end": v(-26.64, -20.86) * mm});
            skLineSegment(sketch, "E679", {"start": v(-26.64, -20.86) * mm, "end": v(-27.64, -21.03) * mm});
            skLineSegment(sketch, "E680", {"start": v(-27.64, -21.03) * mm, "end": v(-28.36, -21.09) * mm});
            skLineSegment(sketch, "E681", {"start": v(-28.36, -21.09) * mm, "end": v(-29.13, -21.08) * mm});
            skLineSegment(sketch, "E682", {"start": v(-29.13, -21.08) * mm, "end": v(-32.44, -23.6) * mm});
            skLineSegment(sketch, "E683", {"start": v(-32.44, -23.6) * mm, "end": v(-33.04, -24.24) * mm});
            skLineSegment(sketch, "E684", {"start": v(-33.04, -24.24) * mm, "end": v(-33.45, -24.8) * mm});
            skLineSegment(sketch, "E685", {"start": v(-33.45, -24.8) * mm, "end": v(-33.72, -25.24) * mm});
            skLineSegment(sketch, "E686", {"start": v(-33.72, -25.24) * mm, "end": v(-33.93, -25.72) * mm});
            skLineSegment(sketch, "E687", {"start": v(-33.93, -25.72) * mm, "end": v(-34.1, -26.22) * mm});
            skLineSegment(sketch, "E688", {"start": v(-34.1, -26.22) * mm, "end": v(-34.19, -26.75) * mm});
            skLineSegment(sketch, "E689", {"start": v(-34.19, -26.75) * mm, "end": v(-34.21, -27.13) * mm});
            skLineSegment(sketch, "E690", {"start": v(-34.21, -27.13) * mm, "end": v(-34.2, -27.52) * mm});
            skLineSegment(sketch, "E691", {"start": v(-34.2, -27.52) * mm, "end": v(-34.19, -27.7) * mm});
            skLineSegment(sketch, "E692", {"start": v(-34.19, -27.7) * mm, "end": v(-34.15, -27.87) * mm});
            skLineSegment(sketch, "E693", {"start": v(-34.15, -27.87) * mm, "end": v(-34.1, -28.03) * mm});
            skLineSegment(sketch, "E694", {"start": v(-34.1, -28.03) * mm, "end": v(-34.02, -28.19) * mm});
            skLineSegment(sketch, "E695", {"start": v(-34.02, -28.19) * mm, "end": v(-33.9, -28.41) * mm});
            skLineSegment(sketch, "E696", {"start": v(-33.9, -28.41) * mm, "end": v(-33.75, -28.62) * mm});
            skLineSegment(sketch, "E697", {"start": v(-33.75, -28.62) * mm, "end": v(-33.46, -28.96) * mm});
            skLineSegment(sketch, "E698", {"start": v(-33.46, -28.96) * mm, "end": v(-32.32, -30.12) * mm});
            skLineSegment(sketch, "E699", {"start": v(-32.32, -30.12) * mm, "end": v(-32.2, -30.3) * mm});
            skLineSegment(sketch, "E700", {"start": v(-32.2, -30.3) * mm, "end": v(-32.12, -30.43) * mm});
            skLineSegment(sketch, "E701", {"start": v(-32.12, -30.43) * mm, "end": v(-32.07, -30.56) * mm});
            skLineSegment(sketch, "E702", {"start": v(-32.07, -30.56) * mm, "end": v(-32.03, -30.7) * mm});
            skLineSegment(sketch, "E703", {"start": v(-32.03, -30.7) * mm, "end": v(-32.02, -30.76) * mm});
            skLineSegment(sketch, "E704", {"start": v(-32.02, -30.76) * mm, "end": v(-32, -30.9) * mm});
            skLineSegment(sketch, "E705", {"start": v(-32, -30.9) * mm, "end": v(-32.02, -31.15) * mm});
            skLineSegment(sketch, "E706", {"start": v(-32.02, -31.15) * mm, "end": v(-32.07, -31.38) * mm});
            skLineSegment(sketch, "E707", {"start": v(-32.07, -31.38) * mm, "end": v(-32.16, -31.6) * mm});
            skLineSegment(sketch, "E708", {"start": v(-32.16, -31.6) * mm, "end": v(-32.28, -31.8) * mm});
            skLineSegment(sketch, "E709", {"start": v(-32.28, -31.8) * mm, "end": v(-32.43, -32) * mm});
            skLineSegment(sketch, "E710", {"start": v(-32.43, -32) * mm, "end": v(-32.7, -32.3) * mm});
            skLineSegment(sketch, "E711", {"start": v(-32.7, -32.3) * mm, "end": v(-33.12, -32.65) * mm});
            skLineSegment(sketch, "E712", {"start": v(-33.12, -32.65) * mm, "end": v(-35.31, -34.28) * mm});
            skLineSegment(sketch, "E713", {"start": v(-35.31, -34.28) * mm, "end": v(-35.61, -34.6) * mm});
            skLineSegment(sketch, "E714", {"start": v(-35.61, -34.6) * mm, "end": v(-35.79, -34.82) * mm});
            skLineSegment(sketch, "E715", {"start": v(-35.79, -34.82) * mm, "end": v(-35.94, -35.06) * mm});
            skLineSegment(sketch, "E716", {"start": v(-35.94, -35.06) * mm, "end": v(-36.06, -35.3) * mm});
            skLineSegment(sketch, "E717", {"start": v(-36.06, -35.3) * mm, "end": v(-36.16, -35.57) * mm});
            skLineSegment(sketch, "E718", {"start": v(-36.16, -35.57) * mm, "end": v(-36.22, -35.85) * mm});
            skLineSegment(sketch, "E719", {"start": v(-36.22, -35.85) * mm, "end": v(-36.24, -36.15) * mm});
            skLineSegment(sketch, "E720", {"start": v(-36.24, -36.15) * mm, "end": v(-36.23, -36.3) * mm});
            skLineSegment(sketch, "E721", {"start": v(-36.23, -36.3) * mm, "end": v(-36.21, -36.43) * mm});
            skLineSegment(sketch, "E722", {"start": v(-36.21, -36.43) * mm, "end": v(-36.16, -36.62) * mm});
            skLineSegment(sketch, "E723", {"start": v(-36.16, -36.62) * mm, "end": v(-36.1, -36.81) * mm});
            skLineSegment(sketch, "E724", {"start": v(-36.1, -36.81) * mm, "end": v(-35.97, -37.06) * mm});
            skLineSegment(sketch, "E725", {"start": v(-35.97, -37.06) * mm, "end": v(-35.73, -37.41) * mm});
            skLineSegment(sketch, "E726", {"start": v(-35.73, -37.41) * mm, "end": v(-35.05, -38.37) * mm});
            skLineSegment(sketch, "E727", {"start": v(-35.05, -38.37) * mm, "end": v(-34.91, -38.64) * mm});
            skLineSegment(sketch, "E728", {"start": v(-34.91, -38.64) * mm, "end": v(-34.83, -38.84) * mm});
            skLineSegment(sketch, "E729", {"start": v(-34.83, -38.84) * mm, "end": v(-34.76, -39.06) * mm});
            skLineSegment(sketch, "E730", {"start": v(-34.76, -39.06) * mm, "end": v(-34.73, -39.21) * mm});
            skLineSegment(sketch, "E731", {"start": v(-34.73, -39.21) * mm, "end": v(-34.71, -39.37) * mm});
            skLineSegment(sketch, "E732", {"start": v(-34.71, -39.37) * mm, "end": v(-34.7, -39.57) * mm});
            skLineSegment(sketch, "E733", {"start": v(-34.7, -39.57) * mm, "end": v(-34.73, -39.85) * mm});
            skLineSegment(sketch, "E734", {"start": v(-34.73, -39.85) * mm, "end": v(-34.78, -40.19) * mm});
            skLineSegment(sketch, "E735", {"start": v(-34.78, -40.19) * mm, "end": v(-35.25, -42.04) * mm});
            skLineSegment(sketch, "E736", {"start": v(-35.25, -42.04) * mm, "end": v(-35.26, -42.27) * mm});
            skLineSegment(sketch, "E737", {"start": v(-35.26, -42.27) * mm, "end": v(-35.25, -42.43) * mm});
            skLineSegment(sketch, "E738", {"start": v(-35.25, -42.43) * mm, "end": v(-35.24, -42.49) * mm});
            skLineSegment(sketch, "E739", {"start": v(-35.24, -42.49) * mm, "end": v(-35.22, -42.59) * mm});
            skLineSegment(sketch, "E740", {"start": v(-35.22, -42.59) * mm, "end": v(-35.14, -42.85) * mm});
            skLineSegment(sketch, "E741", {"start": v(-35.14, -42.85) * mm, "end": v(-35.03, -43.1) * mm});
            skLineSegment(sketch, "E742", {"start": v(-35.03, -43.1) * mm, "end": v(-34.9, -43.33) * mm});
            skLineSegment(sketch, "E743", {"start": v(-34.9, -43.33) * mm, "end": v(-34.67, -43.66) * mm});
            skLineSegment(sketch, "E744", {"start": v(-34.67, -43.66) * mm, "end": v(-34.4, -43.96) * mm});
            skLineSegment(sketch, "E745", {"start": v(-34.4, -43.96) * mm, "end": v(-34.08, -44.25) * mm});
            skLineSegment(sketch, "E746", {"start": v(-34.08, -44.25) * mm, "end": v(-33.63, -44.6) * mm});
            skLineSegment(sketch, "E747", {"start": v(-33.63, -44.6) * mm, "end": v(-31.61, -45.75) * mm});
            skLineSegment(sketch, "E748", {"start": v(-31.61, -45.75) * mm, "end": v(-29.47, -47) * mm});
            skLineSegment(sketch, "E749", {"start": v(-29.47, -47) * mm, "end": v(-29.03, -47.34) * mm});
            skLineSegment(sketch, "E750", {"start": v(-29.03, -47.34) * mm, "end": v(-28.56, -47.79) * mm});
            skLineSegment(sketch, "E751", {"start": v(-28.56, -47.79) * mm, "end": v(-26.6, -49.97) * mm});
            skLineSegment(sketch, "E752", {"start": v(-26.6, -49.97) * mm, "end": v(-26.28, -50.22) * mm});
            skLineSegment(sketch, "E753", {"start": v(-26.28, -50.22) * mm, "end": v(-26.02, -50.4) * mm});
            skLineSegment(sketch, "E754", {"start": v(-26.02, -50.4) * mm, "end": v(-25.74, -50.55) * mm});
            skLineSegment(sketch, "E755", {"start": v(-25.74, -50.55) * mm, "end": v(48.94, -50.55) * mm});
            skLineSegment(sketch, "E756", {"start": v(48.94, -50.55) * mm, "end": v(49.2, -50.43) * mm});
            skLineSegment(sketch, "E757", {"start": v(49.2, -50.43) * mm, "end": v(49.46, -50.3) * mm});
            skLineSegment(sketch, "E758", {"start": v(49.46, -50.3) * mm, "end": v(49.69, -50.13) * mm});
            skLineSegment(sketch, "E759", {"start": v(49.69, -50.13) * mm, "end": v(49.9, -49.95) * mm});
            skLineSegment(sketch, "E760", {"start": v(49.9, -49.95) * mm, "end": v(50.1, -49.75) * mm});
            skLineSegment(sketch, "E761", {"start": v(50.1, -49.75) * mm, "end": v(50.3, -49.49) * mm});
            skLineSegment(sketch, "E762", {"start": v(50.3, -49.49) * mm, "end": v(50.48, -49.2) * mm});
            skLineSegment(sketch, "E763", {"start": v(50.48, -49.2) * mm, "end": v(50.64, -48.9) * mm});
            skLineSegment(sketch, "E764", {"start": v(50.64, -48.9) * mm, "end": v(50.8, -48.51) * mm});
            skLineSegment(sketch, "E765", {"start": v(50.8, -48.51) * mm, "end": v(50.8, 48.51) * mm});
            skLineSegment(sketch, "E766", {"start": v(50.8, 48.51) * mm, "end": v(50.61, 48.95) * mm});
            skLineSegment(sketch, "E767", {"start": v(50.61, 48.95) * mm, "end": v(50.42, 49.3) * mm});
            skLineSegment(sketch, "E768", {"start": v(50.42, 49.3) * mm, "end": v(50.23, 49.58) * mm});
            skLineSegment(sketch, "E769", {"start": v(50.23, 49.58) * mm, "end": v(50.05, 49.8) * mm});
            skLineSegment(sketch, "E770", {"start": v(50.05, 49.8) * mm, "end": v(49.86, 49.99) * mm});
            skLineSegment(sketch, "E771", {"start": v(49.86, 49.99) * mm, "end": v(49.64, 50.16) * mm});
            skLineSegment(sketch, "E772", {"start": v(49.64, 50.16) * mm, "end": v(49.41, 50.32) * mm});
            skLineSegment(sketch, "E773", {"start": v(49.41, 50.32) * mm, "end": v(49.2, 50.43) * mm});
            skLineSegment(sketch, "E774", {"start": v(49.2, 50.43) * mm, "end": v(48.94, 50.55) * mm});
            skLineSegment(sketch, "E775", {"start": v(48.94, 50.55) * mm, "end": v(-48.94, 50.55) * mm});
            skLineSegment(sketch, "E776", {"start": v(-48.94, 50.55) * mm, "end": v(-49.2, 50.43) * mm});
            skLineSegment(sketch, "E777", {"start": v(-49.2, 50.43) * mm, "end": v(-49.46, 50.29) * mm});
            skLineSegment(sketch, "E778", {"start": v(-49.46, 50.29) * mm, "end": v(-49.69, 50.13) * mm});
            skLineSegment(sketch, "E779", {"start": v(-49.69, 50.13) * mm, "end": v(-49.9, 49.95) * mm});
            skLineSegment(sketch, "E780", {"start": v(-49.9, 49.95) * mm, "end": v(-50.1, 49.75) * mm});
            skLineSegment(sketch, "E781", {"start": v(-50.1, 49.75) * mm, "end": v(-50.3, 49.49) * mm});
            skLineSegment(sketch, "E782", {"start": v(-50.3, 49.49) * mm, "end": v(-50.48, 49.2) * mm});
            skLineSegment(sketch, "E783", {"start": v(-50.48, 49.2) * mm, "end": v(-50.64, 48.9) * mm});
            skLineSegment(sketch, "E784", {"start": v(-50.64, 48.9) * mm, "end": v(-50.8, 48.51) * mm});
            skLineSegment(sketch, "E785", {"start": v(-50.8, 48.51) * mm, "end": v(-50.8, -48.51) * mm});
            skLineSegment(sketch, "E786.bottom", {"start": v(57.15, -57.15) * mm, "end": v(-57.15, -57.15) * mm});
            skLineSegment(sketch, "E786.top", {"start": v(57.15, 57.15) * mm, "end": v(-57.15, 57.15) * mm});
            skLineSegment(sketch, "E786.left", {"start": v(57.15, -57.15) * mm, "end": v(57.15, 57.15) * mm});
            skLineSegment(sketch, "E786.right", {"start": v(-57.15, -57.15) * mm, "end": v(-57.15, 57.15) * mm});
            skPoint(sketch, "E786.middle", {"position": v(0, 0) * mm});
            skLineSegment(sketch, "E787", {"start": v(-28.45, -50.55) * mm, "end": v(-25.74, -50.55) * mm});
            skSolve(sketch);
        }
        {
            var Q0;
            Q0=makeQuery(id+"F0.imprint","IMPRINT",FACE,{"disambiguationData":[TD([[makeQuery(id+"F0.imprint","IMPRINT",EDGE,{"derivedFrom":sQuery(id+"F0.wireOp",EDGE,"E0")}),1.0]])]});
            var Q1;
            Q1=makeQuery(id+"F0.imprint","IMPRINT",FACE,{"disambiguationData":[TD([[makeQuery(id+"F0.imprint","IMPRINT",EDGE,{"derivedFrom":sQuery(id+"F0.wireOp",EDGE,"E0")}),-1.0]])]});
            extrude(context, id + "F1", {"entities" : qUnion([Q0, Q1]), "depth" : 1.59 * mm, "offsetDistance" : 25.4 * mm});
        }
        {
            var Q0;
            Q0=makeQuery(id+"F1.opExtrude","SWEPT_EDGE",EDGE,{"disambiguationData":[OSD([sQuery(id+"F0.wireOp",EDGE,"E786.top"),sQuery(id+"F0.wireOp",EDGE,"E786.right")])]});
            var Q1;
            Q1=makeQuery(id+"F1.opExtrude","SWEPT_EDGE",EDGE,{"disambiguationData":[OSD([sQuery(id+"F0.wireOp",EDGE,"E786.top"),sQuery(id+"F0.wireOp",EDGE,"E786.left")])]});
            var Q2;
            Q2=makeQuery(id+"F1.opExtrude","SWEPT_EDGE",EDGE,{"disambiguationData":[OSD([sQuery(id+"F0.wireOp",EDGE,"E786.bottom"),sQuery(id+"F0.wireOp",EDGE,"E786.right")])]});
            var Q3;
            Q3=makeQuery(id+"F1.opExtrude","SWEPT_EDGE",EDGE,{"disambiguationData":[OSD([sQuery(id+"F0.wireOp",EDGE,"E786.bottom"),sQuery(id+"F0.wireOp",EDGE,"E786.left")])]});
            fillet(context, id + "F2", {"entities" : qUnion([Q0, Q1, Q2, Q3]), "radius" : 5.08 * mm, "tangentPropagation" : true, "allowEdgeOverflow" : false});
        }
    });
